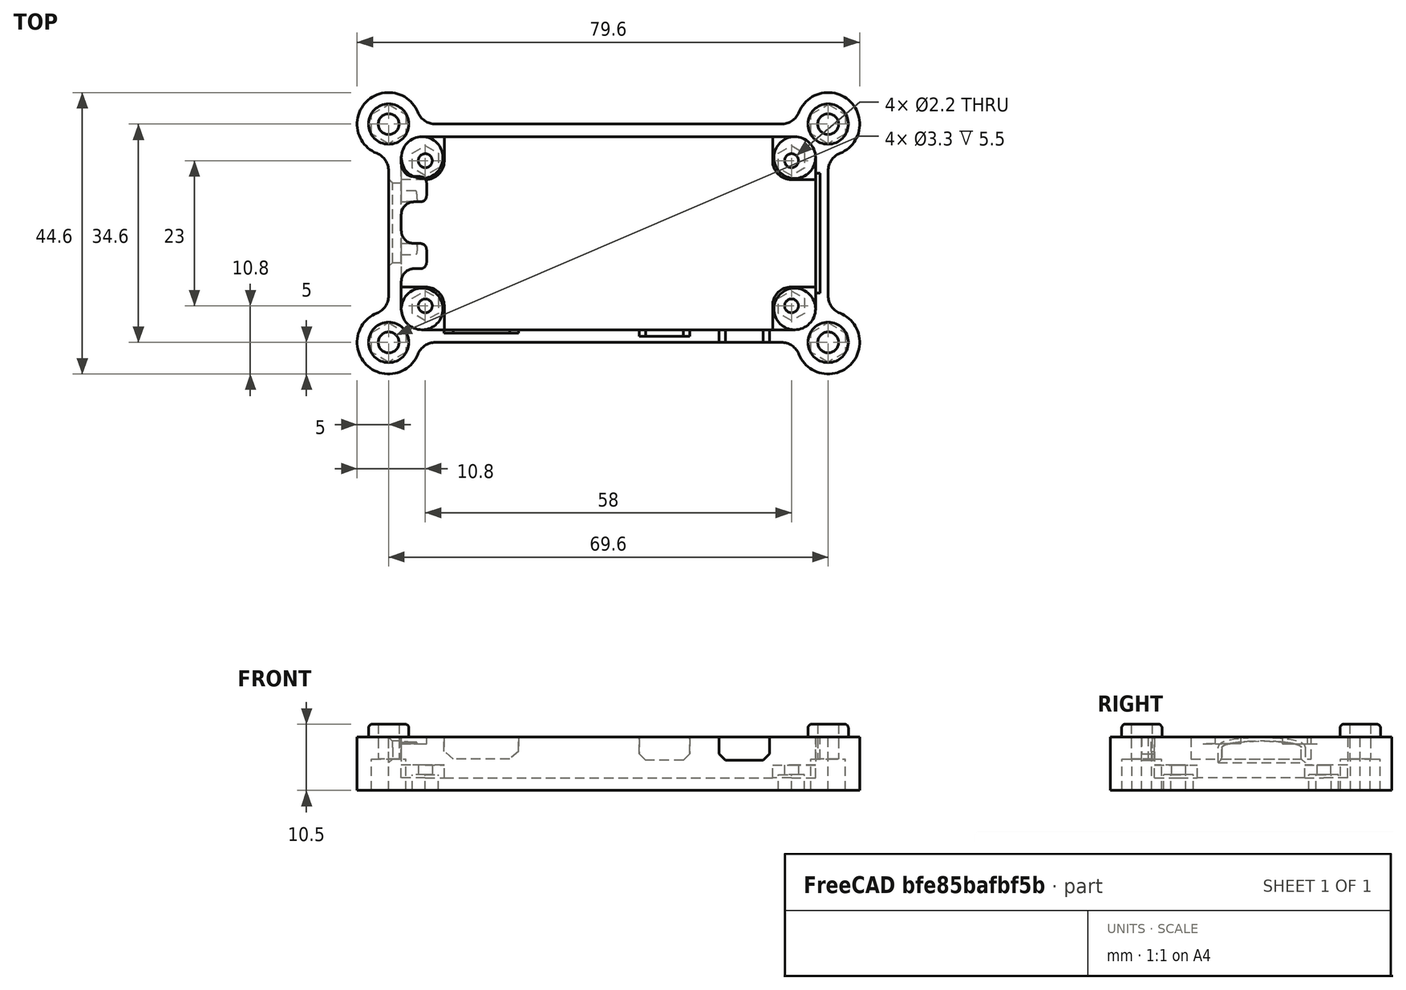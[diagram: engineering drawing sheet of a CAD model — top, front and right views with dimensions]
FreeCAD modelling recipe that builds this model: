
FCSTD DOCUMENT  (FreeCAD 0.18R14111 (Git))
Label: MMDVM_HS_Bottom-SLIM-Single-USB
License: CreativeCommons Attribution-NonCommercial-ShareAlike
LicenseURL: http://creativecommons.org/licenses/by-nc-sa/4.0/
objects: Sketcher::SketchObject×16, PartDesign::Pocket×7, PartDesign::Pad×6, PartDesign::Fillet×5, PartDesign::Hole×2, PartDesign::Chamfer×1, PartDesign::Body×1, Mesh::Feature×1
note: 53 computed .brp shape members not serialized (recipe doc carries the construction recipe); baked Part::Feature solids carry a one-line shape summary decoded from their .brp

FEATURE [Sketcher::SketchObject] Sketch
  MapMode = 5
  Support = -> [XY_Plane]
  sketch-geometry (24):
    g0: LineSegment [constr] StartX=-32.5 StartY=15 StartZ=0 EndX=32.5 EndY=15 EndZ=0
    g1: LineSegment [constr] StartX=32.5 StartY=15 StartZ=0 EndX=32.5 EndY=-15 EndZ=0
    g2: LineSegment [constr] StartX=32.5 StartY=-15 StartZ=0 EndX=-32.5 EndY=-15 EndZ=0
    g3: LineSegment [constr] StartX=-32.5 StartY=-15 StartZ=0 EndX=-32.5 EndY=15 EndZ=0
    g4: LineSegment [constr] StartX=-29 StartY=11.5 StartZ=0 EndX=29 EndY=11.5 EndZ=0
    g5: LineSegment [constr] StartX=29 StartY=11.5 StartZ=0 EndX=29 EndY=-11.5 EndZ=0
    g6: LineSegment [constr] StartX=29 StartY=-11.5 StartZ=0 EndX=-29 EndY=-11.5 EndZ=0
    g7: LineSegment [constr] StartX=-29 StartY=-11.5 StartZ=0 EndX=-29 EndY=11.5 EndZ=0
    g8: Circle CenterX=-29 CenterY=11.5 CenterZ=0 NormalX=0 NormalY=0 NormalZ=1 AngleXU=0 Radius=1.375
    g9: Circle CenterX=29 CenterY=11.5 CenterZ=0 NormalX=0 NormalY=0 NormalZ=1 AngleXU=0 Radius=1.375
    g10: Circle CenterX=29 CenterY=-11.5 CenterZ=0 NormalX=0 NormalY=0 NormalZ=1 AngleXU=0 Radius=1.375
    g11: Circle CenterX=-29 CenterY=-11.5 CenterZ=0 NormalX=0 NormalY=0 NormalZ=1 AngleXU=0 Radius=1.375
    g12: LineSegment [constr] StartX=-29.5 StartY=12 StartZ=0 EndX=29.5 EndY=12 EndZ=0
    g13: LineSegment [constr] StartX=29.5 StartY=12 StartZ=0 EndX=29.5 EndY=-12 EndZ=0
    g14: LineSegment [constr] StartX=29.5 StartY=-12 StartZ=0 EndX=-29.5 EndY=-12 EndZ=0
    g15: LineSegment [constr] StartX=-29.5 StartY=-12 StartZ=0 EndX=-29.5 EndY=12 EndZ=0
    g16: ArcOfCircle CenterX=-29.5 CenterY=12 CenterZ=0 NormalX=0 NormalY=0 NormalZ=1 AngleXU=0 Radius=3 StartAngle=1.5708 EndAngle=3.1416
    g17: ArcOfCircle CenterX=29.5 CenterY=12 CenterZ=0 NormalX=0 NormalY=0 NormalZ=1 AngleXU=0 Radius=3 StartAngle=1.42077e-07 EndAngle=1.5708
    g18: ArcOfCircle CenterX=29.5 CenterY=-12 CenterZ=0 NormalX=0 NormalY=0 NormalZ=1 AngleXU=0 Radius=3 StartAngle=4.71239 EndAngle=6.28319
    g19: ArcOfCircle CenterX=-29.5 CenterY=-12 CenterZ=0 NormalX=0 NormalY=0 NormalZ=1 AngleXU=0 Radius=3 StartAngle=3.14159 EndAngle=4.71239
    g20: LineSegment StartX=-29.5 StartY=15 StartZ=0 EndX=29.5 EndY=15 EndZ=0
    g21: LineSegment StartX=32.5 StartY=12 StartZ=0 EndX=32.5 EndY=-12 EndZ=0
    g22: LineSegment StartX=29.5 StartY=-15 StartZ=0 EndX=-29.5 EndY=-15 EndZ=0
    g23: LineSegment StartX=-32.5 StartY=-12 StartZ=0 EndX=-32.5 EndY=12 EndZ=0
  constraints (68):
    c: Coincident(g0,g1)
    c: Coincident(g1,g2)
    c: Coincident(g2,g3)
    c: Coincident(g3,g0)
    c: Horizontal(g0)
    c: Horizontal(g2)
    c: Vertical(g1)
    c: Vertical(g3)
    c: DistanceX(g0,g0) = 65
    c: DistanceY(g1,g1) = 30
    c: Symmetric(g0,g0,g-2)
    c: Symmetric(g0,g1,g-1)
    c: Coincident(g4,g5)
    c: Coincident(g5,g6)
    c: Coincident(g6,g7)
    c: Coincident(g7,g4)
    c: Horizontal(g4)
    c: Horizontal(g6)
    c: Vertical(g5)
    c: Vertical(g7)
    c: DistanceX(g4,g4) = 58
    c: DistanceY(g5,g5) = 23
    c: Symmetric(g4,g5,g-1)
    c: Symmetric(g4,g4,g-2)
    c: Coincident(g8,g4)
    c: Coincident(g9,g4)
    c: Coincident(g10,g5)
    c: Coincident(g11,g6)
    c: Radius(g11) = 1.375
    c: Radius(g8) = 1.375
    c: Radius(g9) = 1.375
    c: Radius(g10) = 1.375
    c: Coincident(g12,g13)
    c: Coincident(g13,g14)
    c: Coincident(g14,g15)
    c: Coincident(g15,g12)
    c: Horizontal(g12)
    c: Horizontal(g14)
    c: Vertical(g13)
    c: Vertical(g15)
    c: DistanceX(g4,g12) = 0.5
    c: DistanceY(g4,g12) = 0.5
    c: DistanceY(g13,g5) = 0.5
    c: DistanceX(g14,g6) = 0.5
    c: Coincident(g16,g12)
    c: Radius(g16) = 3
    c: Coincident(g17,g12)
    c: Radius(g17) = 3
    c: Coincident(g18,g13)
    c: Radius(g18) = 3
    c: Coincident(g19,g14)
    c: Radius(g19) = 3
    c: PointOnObject(g16,g0)
    c: PointOnObject(g17,g1)
    c: PointOnObject(g18,g2)
    c: PointOnObject(g19,g3)
    c: Coincident(g20,g16)
    c: Horizontal(g20)
    c: Coincident(g20,g17)
    c: Coincident(g21,g17)
    c: Vertical(g21)
    c: Coincident(g18,g21)
    c: Coincident(g22,g18)
    c: Horizontal(g22)
    c: Coincident(g19,g22)
    c: Coincident(g23,g19)
    c: Vertical(g23)
    c: Coincident(g23,g16)
FEATURE [Sketcher::SketchObject] Sketch001
  MapMode = 5
  Support = -> [XY_Plane]
  expr: Constraints[8] = Sketch.Constraints[8]
  expr: Constraints[41] = Sketch.Constraints[41]
  expr: Constraints[9] = Sketch.Constraints[9]
  expr: Constraints[45] = Sketch.Constraints[45]
  expr: Constraints[43] = Sketch.Constraints[43]
  expr: Constraints[42] = Sketch.Constraints[42]
  expr: Constraints[20] = Sketch.Constraints[20]
  expr: Constraints[21] = Sketch.Constraints[21]
  expr: Constraints[28] = Sketch.Constraints[28]
  expr: Constraints[29] = Sketch.Constraints[29]
  expr: Constraints[30] = Sketch.Constraints[30]
  expr: Constraints[40] = Sketch.Constraints[40]
  expr: Constraints[31] = Sketch.Constraints[31]
  expr: Constraints[47] = Sketch.Constraints[47]
  expr: Constraints[49] = Sketch.Constraints[49]
  expr: Constraints[51] = Sketch.Constraints[51]
  sketch-geometry (64):
    g0: LineSegment [constr] StartX=-32.5 StartY=15 StartZ=0 EndX=32.5 EndY=15 EndZ=0
    g1: LineSegment [constr] StartX=32.5 StartY=15 StartZ=0 EndX=32.5 EndY=-15 EndZ=0
    g2: LineSegment [constr] StartX=32.5 StartY=-15 StartZ=0 EndX=-32.5 EndY=-15 EndZ=0
    g3: LineSegment [constr] StartX=-32.5 StartY=-15 StartZ=0 EndX=-32.5 EndY=15 EndZ=0
    g4: LineSegment [constr] StartX=-29 StartY=11.5 StartZ=0 EndX=29 EndY=11.5 EndZ=0
    g5: LineSegment [constr] StartX=29 StartY=11.5 StartZ=0 EndX=29 EndY=-11.5 EndZ=0
    g6: LineSegment [constr] StartX=29 StartY=-11.5 StartZ=0 EndX=-29 EndY=-11.5 EndZ=0
    g7: LineSegment [constr] StartX=-29 StartY=-11.5 StartZ=0 EndX=-29 EndY=11.5 EndZ=0
    g8: Circle [constr] CenterX=-29 CenterY=11.5 CenterZ=0 NormalX=0 NormalY=0 NormalZ=1 AngleXU=0 Radius=1.375
    g9: Circle [constr] CenterX=29 CenterY=11.5 CenterZ=0 NormalX=0 NormalY=0 NormalZ=1 AngleXU=0 Radius=1.375
    g10: Circle [constr] CenterX=29 CenterY=-11.5 CenterZ=0 NormalX=0 NormalY=0 NormalZ=1 AngleXU=0 Radius=1.375
    g11: Circle [constr] CenterX=-29 CenterY=-11.5 CenterZ=0 NormalX=0 NormalY=0 NormalZ=1 AngleXU=0 Radius=1.375
    g12: LineSegment [constr] StartX=-29.5 StartY=12 StartZ=0 EndX=29.5 EndY=12 EndZ=0
    g13: LineSegment [constr] StartX=29.5 StartY=12 StartZ=0 EndX=29.5 EndY=-12 EndZ=0
    g14: LineSegment [constr] StartX=29.5 StartY=-12 StartZ=0 EndX=-29.5 EndY=-12 EndZ=0
    g15: LineSegment [constr] StartX=-29.5 StartY=-12 StartZ=0 EndX=-29.5 EndY=12 EndZ=0
    g16: ArcOfCircle [constr] CenterX=-29.5 CenterY=12 CenterZ=0 NormalX=0 NormalY=0 NormalZ=1 AngleXU=0 Radius=3 StartAngle=1.5708 EndAngle=3.14159
    g17: ArcOfCircle [constr] CenterX=29.5 CenterY=12 CenterZ=0 NormalX=0 NormalY=0 NormalZ=1 AngleXU=0 Radius=3 StartAngle=2.8425e-08 EndAngle=1.5708
    g18: ArcOfCircle [constr] CenterX=29.5 CenterY=-12 CenterZ=0 NormalX=0 NormalY=0 NormalZ=1 AngleXU=0 Radius=3 StartAngle=4.71239 EndAngle=6.28319
    g19: ArcOfCircle [constr] CenterX=-29.5 CenterY=-12 CenterZ=0 NormalX=0 NormalY=0 NormalZ=1 AngleXU=0 Radius=3 StartAngle=3.14159 EndAngle=4.71239
    g20: LineSegment [constr] StartX=-29.5 StartY=15 StartZ=0 EndX=29.5 EndY=15 EndZ=0
    g21: LineSegment [constr] StartX=32.5 StartY=12 StartZ=0 EndX=32.5 EndY=-12 EndZ=0
    g22: LineSegment [constr] StartX=29.5 StartY=-15 StartZ=0 EndX=-29.5 EndY=-15 EndZ=0
    g23: LineSegment [constr] StartX=-32.5 StartY=-12 StartZ=0 EndX=-32.5 EndY=12 EndZ=0
    g24: ArcOfCircle [constr] CenterX=-29.5 CenterY=12 CenterZ=0 NormalX=0 NormalY=0 NormalZ=1 AngleXU=0 Radius=3.3 StartAngle=1.5708 EndAngle=3.14159
    g25: ArcOfCircle [constr] CenterX=29.5 CenterY=12 CenterZ=0 NormalX=0 NormalY=0 NormalZ=1 AngleXU=0 Radius=3.3 StartAngle=-2.2e-10 EndAngle=1.5708
    g26: ArcOfCircle [constr] CenterX=29.5 CenterY=-12 CenterZ=0 NormalX=0 NormalY=0 NormalZ=1 AngleXU=0 Radius=3.3 StartAngle=4.71239 EndAngle=6.28319
    g27: ArcOfCircle [constr] CenterX=-29.5 CenterY=-12 CenterZ=0 NormalX=0 NormalY=0 NormalZ=1 AngleXU=0 Radius=3.3 StartAngle=3.14159 EndAngle=4.71239
    g28: LineSegment [constr] StartX=-32.8 StartY=12 StartZ=0 EndX=-32.8 EndY=-12 EndZ=0
    g29: LineSegment [constr] StartX=-29.5 StartY=15.3 StartZ=0 EndX=29.5 EndY=15.3 EndZ=0
    g30: LineSegment [constr] StartX=32.8 StartY=12 StartZ=0 EndX=32.8 EndY=-12 EndZ=0
    g31: LineSegment [constr] StartX=29.5 StartY=-15.3 StartZ=0 EndX=-29.5 EndY=-15.3 EndZ=0
    g32: LineSegment [constr] StartX=-34.8 StartY=17.3 StartZ=0 EndX=34.8 EndY=17.3 EndZ=0
    g33: LineSegment [constr] StartX=34.8 StartY=17.3 StartZ=0 EndX=34.8 EndY=-17.3 EndZ=0
    g34: LineSegment [constr] StartX=34.8 StartY=-17.3 StartZ=0 EndX=-34.8 EndY=-17.3 EndZ=0
    g35: LineSegment [constr] StartX=-34.8 StartY=-17.3 StartZ=0 EndX=-34.8 EndY=17.3 EndZ=0
    g36: Circle [constr] CenterX=34.8 CenterY=17.3 CenterZ=0 NormalX=0 NormalY=0 NormalZ=1 AngleXU=0 Radius=5
    g37: Circle [constr] CenterX=34.8 CenterY=-17.3 CenterZ=0 NormalX=0 NormalY=0 NormalZ=1 AngleXU=0 Radius=5
    g38: Circle [constr] CenterX=-34.8 CenterY=-17.3 CenterZ=0 NormalX=0 NormalY=0 NormalZ=1 AngleXU=0 Radius=5
    g39: Circle [constr] CenterX=-34.8 CenterY=17.3 CenterZ=0 NormalX=0 NormalY=0 NormalZ=1 AngleXU=0 Radius=5
    g40: Circle [constr] CenterX=27.3838 CenterY=20.3 CenterZ=0 NormalX=0 NormalY=0 NormalZ=1 AngleXU=0 Radius=3
    g41: Circle [constr] CenterX=-27.3838 CenterY=20.3 CenterZ=0 NormalX=0 NormalY=0 NormalZ=1 AngleXU=0 Radius=3
    g42: Circle [constr] CenterX=-37.8 CenterY=9.8838 CenterZ=0 NormalX=0 NormalY=0 NormalZ=1 AngleXU=0 Radius=3
    g43: Circle [constr] CenterX=-37.8 CenterY=-9.8838 CenterZ=0 NormalX=0 NormalY=0 NormalZ=1 AngleXU=0 Radius=3
    g44: Circle [constr] CenterX=-27.3838 CenterY=-20.3 CenterZ=0 NormalX=0 NormalY=0 NormalZ=1 AngleXU=0 Radius=3
    g45: Circle [constr] CenterX=27.3838 CenterY=-20.3 CenterZ=0 NormalX=0 NormalY=0 NormalZ=1 AngleXU=0 Radius=3
    g46: Circle [constr] CenterX=37.8 CenterY=-9.8838 CenterZ=0 NormalX=0 NormalY=0 NormalZ=1 AngleXU=0 Radius=3
    g47: Circle [constr] CenterX=37.8 CenterY=9.8838 CenterZ=0 NormalX=0 NormalY=0 NormalZ=1 AngleXU=0 Radius=3
    g48: ArcOfCircle CenterX=34.8 CenterY=17.3 CenterZ=0 NormalX=0 NormalY=0 NormalZ=1 AngleXU=0 Radius=5 StartAngle=5.09679 EndAngle=9.04038
    g49: ArcOfCircle CenterX=27.3838 CenterY=20.3 CenterZ=0 NormalX=0 NormalY=0 NormalZ=1 AngleXU=0 Radius=3 StartAngle=4.71239 EndAngle=5.89879
    g50: ArcOfCircle CenterX=37.8 CenterY=9.8838 CenterZ=0 NormalX=0 NormalY=0 NormalZ=1 AngleXU=0 Radius=3 StartAngle=1.95519 EndAngle=3.14159
    g51: ArcOfCircle CenterX=37.8 CenterY=-9.8838 CenterZ=0 NormalX=0 NormalY=0 NormalZ=1 AngleXU=0 Radius=3 StartAngle=3.14159 EndAngle=4.32799
    g52: ArcOfCircle CenterX=34.8 CenterY=-17.3 CenterZ=0 NormalX=0 NormalY=0 NormalZ=1 AngleXU=0 Radius=5 StartAngle=3.52599 EndAngle=7.46958
    g53: ArcOfCircle CenterX=27.3838 CenterY=-20.3 CenterZ=0 NormalX=0 NormalY=0 NormalZ=1 AngleXU=0 Radius=3 StartAngle=0.384397 EndAngle=1.5708
    g54: ArcOfCircle CenterX=-27.3838 CenterY=-20.3 CenterZ=0 NormalX=0 NormalY=0 NormalZ=1 AngleXU=0 Radius=3 StartAngle=1.5708 EndAngle=2.7572
    g55: ArcOfCircle CenterX=-34.8 CenterY=-17.3 CenterZ=0 NormalX=0 NormalY=0 NormalZ=1 AngleXU=0 Radius=5 StartAngle=1.95519 EndAngle=5.89879
    g56: ArcOfCircle CenterX=-37.8 CenterY=-9.8838 CenterZ=0 NormalX=0 NormalY=0 NormalZ=1 AngleXU=0 Radius=3 StartAngle=5.09679 EndAngle=6.28319
    g57: ArcOfCircle CenterX=-37.8 CenterY=9.8838 CenterZ=0 NormalX=0 NormalY=0 NormalZ=1 AngleXU=0 Radius=3 StartAngle=6.28319 EndAngle=7.46958
    g58: ArcOfCircle CenterX=-34.8 CenterY=17.3 CenterZ=0 NormalX=0 NormalY=0 NormalZ=1 AngleXU=0 Radius=5 StartAngle=0.384397 EndAngle=4.32799
    g59: ArcOfCircle CenterX=-27.3838 CenterY=20.3 CenterZ=0 NormalX=0 NormalY=0 NormalZ=1 AngleXU=0 Radius=3 StartAngle=3.52599 EndAngle=4.71239
    g60: LineSegment StartX=-27.3838 StartY=17.3 StartZ=0 EndX=27.3838 EndY=17.3 EndZ=0
    g61: LineSegment StartX=34.8 StartY=9.8838 StartZ=0 EndX=34.8 EndY=-9.8838 EndZ=0
    g62: LineSegment StartX=27.3838 StartY=-17.3 StartZ=0 EndX=-27.3838 EndY=-17.3 EndZ=0
    g63: LineSegment StartX=-34.8 StartY=-9.8838 StartZ=0 EndX=-34.8 EndY=9.8838 EndZ=0
  constraints (184):
    c: Coincident(g0,g1)
    c: Coincident(g1,g2)
    c: Coincident(g2,g3)
    c: Coincident(g3,g0)
    c: Horizontal(g0)
    c: Horizontal(g2)
    c: Vertical(g1)
    c: Vertical(g3)
    c: DistanceX(g0,g0) = 65
    c: DistanceY(g1,g1) = 30
    c: Symmetric(g0,g0,g-2)
    c: Symmetric(g0,g1,g-1)
    c: Coincident(g4,g5)
    c: Coincident(g5,g6)
    c: Coincident(g6,g7)
    c: Coincident(g7,g4)
    c: Horizontal(g4)
    c: Horizontal(g6)
    c: Vertical(g5)
    c: Vertical(g7)
    c: DistanceX(g4,g4) = 58
    c: DistanceY(g5,g5) = 23
    c: Symmetric(g4,g5,g-1)
    c: Symmetric(g4,g4,g-2)
    c: Coincident(g8,g4)
    c: Coincident(g9,g4)
    c: Coincident(g10,g5)
    c: Coincident(g11,g6)
    c: Radius(g11) = 1.375
    c: Radius(g8) = 1.375
    c: Radius(g9) = 1.375
    c: Radius(g10) = 1.375
    c: Coincident(g12,g13)
    c: Coincident(g13,g14)
    c: Coincident(g14,g15)
    c: Coincident(g15,g12)
    c: Horizontal(g12)
    c: Horizontal(g14)
    c: Vertical(g13)
    c: Vertical(g15)
    c: DistanceX(g4,g12) = 0.5
    c: DistanceY(g4,g12) = 0.5
    c: DistanceY(g13,g5) = 0.5
    c: DistanceX(g14,g6) = 0.5
    c: Coincident(g16,g12)
    c: Radius(g16) = 3
    c: Coincident(g17,g12)
    c: Radius(g17) = 3
    c: Coincident(g18,g13)
    c: Radius(g18) = 3
    c: Coincident(g19,g14)
    c: Radius(g19) = 3
    c: PointOnObject(g16,g0)
    c: PointOnObject(g17,g1)
    c: PointOnObject(g18,g2)
    c: PointOnObject(g19,g3)
    c: Coincident(g20,g16)
    c: Horizontal(g20)
    c: Coincident(g20,g17)
    c: Coincident(g21,g17)
    c: Vertical(g21)
    c: Coincident(g18,g21)
    c: Coincident(g22,g18)
    c: Horizontal(g22)
    c: Coincident(g19,g22)
    c: Coincident(g23,g19)
    c: Vertical(g23)
    c: Coincident(g23,g16)
    c: Coincident(g24,g12)
    c: Radius(g24) = 3.3
    c: Coincident(g25,g12)
    c: Radius(g25) = 3.3
    c: Coincident(g26,g13)
    c: Radius(g26) = 3.3
    c: Coincident(g27,g14)
    c: Radius(g27) = 3.3
    c: Vertical(g28)
    c: DistanceX(g28,g2) = 0.3
    c: Coincident(g27,g28)
    c: Coincident(g28,g24)
    c: Horizontal(g29)
    c: DistanceY(g0,g29) = 0.3
    c: Coincident(g24,g29)
    c: Coincident(g25,g29)
    c: Vertical(g30)
    c: DistanceX(g0,g30) = 0.3
    c: Coincident(g25,g30)
    c: Coincident(g30,g26)
    c: Horizontal(g31)
    c: DistanceY(g31,g1) = 0.3
    c: Coincident(g31,g26)
    c: Coincident(g31,g27)
    c: Coincident(g32,g33)
    c: Coincident(g33,g34)
    c: Coincident(g34,g35)
    c: Coincident(g35,g32)
    c: Horizontal(g32)
    c: Horizontal(g34)
    c: Vertical(g33)
    c: Vertical(g35)
    c: DistanceY(g25,g32) = 2
    c: DistanceX(g25,g32) = 2
    c: DistanceY(g33,g26) = 2
    c: DistanceX(g34,g27) = 2
    c: Coincident(g36,g32)
    c: Coincident(g37,g33)
    c: Coincident(g38,g34)
    c: Coincident(g39,g32)
    c: Radius(g39) = 5
    c: Radius(g38) = 5
    c: Radius(g37) = 5
    c: Radius(g36) = 5
    c: Radius(g40) = 3
    c: Tangent(g40,g36)
    c: Tangent(g40,g32)
    c: Tangent(g47,g36)
    c: Radius(g47) = 3
    c: Tangent(g47,g33)
    c: Radius(g46) = 3
    c: Tangent(g46,g37)
    c: Tangent(g46,g33)
    c: Radius(g45) = 3
    c: Tangent(g45,g37)
    c: Tangent(g45,g34)
    c: Radius(g44) = 3
    c: Tangent(g44,g34)
    c: Tangent(g44,g38)
    c: Radius(g43) = 3
    c: Tangent(g43,g38)
    c: Tangent(g43,g35)
    c: Radius(g42) = 3
    c: Tangent(g42,g35)
    c: Tangent(g42,g39)
    c: Radius(g41) = 3
    c: Tangent(g41,g32)
    c: Tangent(g41,g39)
    c: Coincident(g48,g32)
    c: PointOnObject(g48,g36)
    c: Coincident(g49,g40)
    c: PointOnObject(g49,g40)
    c: Coincident(g50,g47)
    c: PointOnObject(g50,g47)
    c: Coincident(g51,g46)
    c: PointOnObject(g51,g46)
    c: Coincident(g52,g33)
    c: PointOnObject(g52,g37)
    c: Coincident(g53,g45)
    c: PointOnObject(g53,g45)
    c: Coincident(g54,g44)
    c: PointOnObject(g54,g44)
    c: Coincident(g55,g34)
    c: PointOnObject(g55,g38)
    c: Coincident(g56,g43)
    c: PointOnObject(g56,g43)
    c: Coincident(g57,g42)
    c: PointOnObject(g57,g42)
    c: Coincident(g58,g32)
    c: PointOnObject(g58,g39)
    c: Coincident(g59,g41)
    c: PointOnObject(g59,g41)
    c: Coincident(g49,g48)
    c: Coincident(g48,g50)
    c: Coincident(g51,g52)
    c: Coincident(g52,g53)
    c: Coincident(g54,g55)
    c: Coincident(g55,g56)
    c: Coincident(g57,g58)
    c: Coincident(g58,g59)
    c: PointOnObject(g60,g32)
    c: Horizontal(g60)
    c: PointOnObject(g61,g33)
    c: Vertical(g61)
    c: PointOnObject(g62,g34)
    c: Horizontal(g62)
    c: PointOnObject(g63,g35)
    c: Vertical(g63)
    c: Coincident(g59,g60)
    c: Coincident(g60,g49)
    c: Coincident(g50,g61)
    c: Coincident(g61,g51)
    c: Coincident(g53,g62)
    c: Coincident(g54,g62)
    c: Coincident(g56,g63)
    c: Coincident(g57,g63)
FEATURE [PartDesign::Pad] Pad
  Length = 8.5
  Length2 = 100
  Profile = -> Sketch001
  Type = 0
FEATURE [Sketcher::SketchObject] Sketch002
  MapMode = 5
  Placement = pos=(0,0,8.5) rot=(0,0,1;0rad)
  Support = -> [Pad]
  expr: Constraints[133] = Sketch001.Constraints[133]
  expr: Constraints[130] = Sketch001.Constraints[130]
  expr: Constraints[112] = Sketch001.Constraints[112]
  expr: Constraints[124] = Sketch001.Constraints[124]
  expr: Constraints[127] = Sketch001.Constraints[127]
  expr: Constraints[110] = Sketch001.Constraints[110]
  expr: Constraints[51] = Sketch001.Constraints[51]
  expr: Constraints[100] = Sketch001.Constraints[100]
  expr: Constraints[77] = Sketch001.Constraints[77]
  expr: Constraints[89] = Sketch001.Constraints[89]
  expr: Constraints[85] = Sketch001.Constraints[85]
  expr: Constraints[118] = Sketch001.Constraints[118]
  expr: Constraints[71] = Sketch001.Constraints[71]
  expr: Constraints[111] = Sketch001.Constraints[111]
  expr: Constraints[103] = Sketch001.Constraints[103]
  expr: Constraints[49] = Sketch001.Constraints[49]
  expr: Constraints[102] = Sketch001.Constraints[102]
  expr: Constraints[69] = Sketch001.Constraints[69]
  expr: Constraints[47] = Sketch001.Constraints[47]
  expr: Constraints[73] = Sketch001.Constraints[73]
  expr: Constraints[75] = Sketch001.Constraints[75]
  expr: Constraints[31] = Sketch001.Constraints[31]
  expr: Constraints[116] = Sketch001.Constraints[116]
  expr: Constraints[40] = Sketch001.Constraints[40]
  expr: Constraints[30] = Sketch001.Constraints[30]
  expr: Constraints[29] = Sketch001.Constraints[29]
  expr: Constraints[28] = Sketch001.Constraints[28]
  expr: Constraints[121] = Sketch001.Constraints[121]
  expr: Constraints[21] = Sketch001.Constraints[21]
  expr: Constraints[20] = Sketch001.Constraints[20]
  expr: Constraints[43] = Sketch001.Constraints[43]
  expr: Constraints[42] = Sketch001.Constraints[42]
  expr: Constraints[101] = Sketch001.Constraints[101]
  expr: Constraints[108] = Sketch001.Constraints[108]
  expr: Constraints[45] = Sketch001.Constraints[45]
  expr: Constraints[41] = Sketch001.Constraints[41]
  expr: Constraints[9] = Sketch001.Constraints[9]
  expr: Constraints[81] = Sketch001.Constraints[81]
  expr: Constraints[109] = Sketch001.Constraints[109]
  expr: Constraints[8] = Sketch001.Constraints[8]
  sketch-geometry (64):
    g0: LineSegment [constr] StartX=-32.5 StartY=15 StartZ=0 EndX=32.5 EndY=15 EndZ=0
    g1: LineSegment [constr] StartX=32.5 StartY=15 StartZ=0 EndX=32.5 EndY=-15 EndZ=0
    g2: LineSegment [constr] StartX=32.5 StartY=-15 StartZ=0 EndX=-32.5 EndY=-15 EndZ=0
    g3: LineSegment [constr] StartX=-32.5 StartY=-15 StartZ=0 EndX=-32.5 EndY=15 EndZ=0
    g4: LineSegment [constr] StartX=-29 StartY=11.5 StartZ=0 EndX=29 EndY=11.5 EndZ=0
    g5: LineSegment [constr] StartX=29 StartY=11.5 StartZ=0 EndX=29 EndY=-11.5 EndZ=0
    g6: LineSegment [constr] StartX=29 StartY=-11.5 StartZ=0 EndX=-29 EndY=-11.5 EndZ=0
    g7: LineSegment [constr] StartX=-29 StartY=-11.5 StartZ=0 EndX=-29 EndY=11.5 EndZ=0
    g8: Circle [constr] CenterX=-29 CenterY=11.5 CenterZ=0 NormalX=0 NormalY=0 NormalZ=1 AngleXU=0 Radius=1.375
    g9: Circle [constr] CenterX=29 CenterY=11.5 CenterZ=0 NormalX=0 NormalY=0 NormalZ=1 AngleXU=0 Radius=1.375
    g10: Circle [constr] CenterX=29 CenterY=-11.5 CenterZ=0 NormalX=0 NormalY=0 NormalZ=1 AngleXU=0 Radius=1.375
    g11: Circle [constr] CenterX=-29 CenterY=-11.5 CenterZ=0 NormalX=0 NormalY=0 NormalZ=1 AngleXU=0 Radius=1.375
    g12: LineSegment [constr] StartX=-29.5 StartY=12 StartZ=0 EndX=29.5 EndY=12 EndZ=0
    g13: LineSegment [constr] StartX=29.5 StartY=12 StartZ=0 EndX=29.5 EndY=-12 EndZ=0
    g14: LineSegment [constr] StartX=29.5 StartY=-12 StartZ=0 EndX=-29.5 EndY=-12 EndZ=0
    g15: LineSegment [constr] StartX=-29.5 StartY=-12 StartZ=0 EndX=-29.5 EndY=12 EndZ=0
    g16: ArcOfCircle [constr] CenterX=-29.5 CenterY=12 CenterZ=0 NormalX=0 NormalY=0 NormalZ=1 AngleXU=0 Radius=3 StartAngle=1.5708 EndAngle=3.14159
    g17: ArcOfCircle [constr] CenterX=29.5 CenterY=12 CenterZ=0 NormalX=0 NormalY=0 NormalZ=1 AngleXU=0 Radius=3 StartAngle=2.8425e-08 EndAngle=1.5708
    g18: ArcOfCircle [constr] CenterX=29.5 CenterY=-12 CenterZ=0 NormalX=0 NormalY=0 NormalZ=1 AngleXU=0 Radius=3 StartAngle=4.71239 EndAngle=6.28319
    g19: ArcOfCircle [constr] CenterX=-29.5 CenterY=-12 CenterZ=0 NormalX=0 NormalY=0 NormalZ=1 AngleXU=0 Radius=3 StartAngle=3.14159 EndAngle=4.71239
    g20: LineSegment [constr] StartX=-29.5 StartY=15 StartZ=0 EndX=29.5 EndY=15 EndZ=0
    g21: LineSegment [constr] StartX=32.5 StartY=12 StartZ=0 EndX=32.5 EndY=-12 EndZ=0
    g22: LineSegment [constr] StartX=29.5 StartY=-15 StartZ=0 EndX=-29.5 EndY=-15 EndZ=0
    g23: LineSegment [constr] StartX=-32.5 StartY=-12 StartZ=0 EndX=-32.5 EndY=12 EndZ=0
    g24: ArcOfCircle CenterX=-29.5 CenterY=12 CenterZ=0 NormalX=0 NormalY=0 NormalZ=1 AngleXU=0 Radius=3.3 StartAngle=1.5708 EndAngle=3.14159
    g25: ArcOfCircle CenterX=29.5 CenterY=12 CenterZ=0 NormalX=0 NormalY=0 NormalZ=1 AngleXU=0 Radius=3.3 StartAngle=-2.2e-10 EndAngle=1.5708
    g26: ArcOfCircle CenterX=29.5 CenterY=-12 CenterZ=0 NormalX=0 NormalY=0 NormalZ=1 AngleXU=0 Radius=3.3 StartAngle=4.71239 EndAngle=6.28319
    g27: ArcOfCircle CenterX=-29.5 CenterY=-12 CenterZ=0 NormalX=0 NormalY=0 NormalZ=1 AngleXU=0 Radius=3.3 StartAngle=3.14159 EndAngle=4.71239
    g28: LineSegment StartX=-32.8 StartY=12 StartZ=0 EndX=-32.8 EndY=-12 EndZ=0
    g29: LineSegment StartX=-29.5 StartY=15.3 StartZ=0 EndX=29.5 EndY=15.3 EndZ=0
    g30: LineSegment StartX=32.8 StartY=12 StartZ=0 EndX=32.8 EndY=-12 EndZ=0
    g31: LineSegment StartX=29.5 StartY=-15.3 StartZ=0 EndX=-29.5 EndY=-15.3 EndZ=0
    g32: LineSegment [constr] StartX=-34.8 StartY=17.3 StartZ=0 EndX=34.8 EndY=17.3 EndZ=0
    g33: LineSegment [constr] StartX=34.8 StartY=17.3 StartZ=0 EndX=34.8 EndY=-17.3 EndZ=0
    g34: LineSegment [constr] StartX=34.8 StartY=-17.3 StartZ=0 EndX=-34.8 EndY=-17.3 EndZ=0
    g35: LineSegment [constr] StartX=-34.8 StartY=-17.3 StartZ=0 EndX=-34.8 EndY=17.3 EndZ=0
    g36: Circle [constr] CenterX=34.8 CenterY=17.3 CenterZ=0 NormalX=0 NormalY=0 NormalZ=1 AngleXU=0 Radius=5
    g37: Circle [constr] CenterX=34.8 CenterY=-17.3 CenterZ=0 NormalX=0 NormalY=0 NormalZ=1 AngleXU=0 Radius=5
    g38: Circle [constr] CenterX=-34.8 CenterY=-17.3 CenterZ=0 NormalX=0 NormalY=0 NormalZ=1 AngleXU=0 Radius=5
    g39: Circle [constr] CenterX=-34.8 CenterY=17.3 CenterZ=0 NormalX=0 NormalY=0 NormalZ=1 AngleXU=0 Radius=5
    g40: Circle [constr] CenterX=27.3838 CenterY=20.3 CenterZ=0 NormalX=0 NormalY=0 NormalZ=1 AngleXU=0 Radius=3
    g41: Circle [constr] CenterX=-27.3838 CenterY=20.3 CenterZ=0 NormalX=0 NormalY=0 NormalZ=1 AngleXU=0 Radius=3
    g42: Circle [constr] CenterX=-37.8 CenterY=9.8838 CenterZ=0 NormalX=0 NormalY=0 NormalZ=1 AngleXU=0 Radius=3
    g43: Circle [constr] CenterX=-37.8 CenterY=-9.8838 CenterZ=0 NormalX=0 NormalY=0 NormalZ=1 AngleXU=0 Radius=3
    g44: Circle [constr] CenterX=-27.3838 CenterY=-20.3 CenterZ=0 NormalX=0 NormalY=0 NormalZ=1 AngleXU=0 Radius=3
    g45: Circle [constr] CenterX=27.3838 CenterY=-20.3 CenterZ=0 NormalX=0 NormalY=0 NormalZ=1 AngleXU=0 Radius=3
    g46: Circle [constr] CenterX=37.8 CenterY=-9.8838 CenterZ=0 NormalX=0 NormalY=0 NormalZ=1 AngleXU=0 Radius=3
    g47: Circle [constr] CenterX=37.8 CenterY=9.8838 CenterZ=0 NormalX=0 NormalY=0 NormalZ=1 AngleXU=0 Radius=3
    g48: ArcOfCircle [constr] CenterX=34.8 CenterY=17.3 CenterZ=0 NormalX=0 NormalY=0 NormalZ=1 AngleXU=0 Radius=5 StartAngle=5.09679 EndAngle=9.04038
    g49: ArcOfCircle [constr] CenterX=27.3838 CenterY=20.3 CenterZ=0 NormalX=0 NormalY=0 NormalZ=1 AngleXU=0 Radius=3 StartAngle=4.71239 EndAngle=5.89879
    g50: ArcOfCircle [constr] CenterX=37.8 CenterY=9.8838 CenterZ=0 NormalX=0 NormalY=0 NormalZ=1 AngleXU=0 Radius=3 StartAngle=1.95519 EndAngle=3.14159
    g51: ArcOfCircle [constr] CenterX=37.8 CenterY=-9.8838 CenterZ=0 NormalX=0 NormalY=0 NormalZ=1 AngleXU=0 Radius=3 StartAngle=3.14159 EndAngle=4.32799
    g52: ArcOfCircle [constr] CenterX=34.8 CenterY=-17.3 CenterZ=0 NormalX=0 NormalY=0 NormalZ=1 AngleXU=0 Radius=5 StartAngle=3.52599 EndAngle=7.46958
    g53: ArcOfCircle [constr] CenterX=27.3838 CenterY=-20.3 CenterZ=0 NormalX=0 NormalY=0 NormalZ=1 AngleXU=0 Radius=3 StartAngle=0.384397 EndAngle=1.5708
    g54: ArcOfCircle [constr] CenterX=-27.3838 CenterY=-20.3 CenterZ=0 NormalX=0 NormalY=0 NormalZ=1 AngleXU=0 Radius=3 StartAngle=1.5708 EndAngle=2.7572
    g55: ArcOfCircle [constr] CenterX=-34.8 CenterY=-17.3 CenterZ=0 NormalX=0 NormalY=0 NormalZ=1 AngleXU=0 Radius=5 StartAngle=1.95519 EndAngle=5.89879
    g56: ArcOfCircle [constr] CenterX=-37.8 CenterY=-9.8838 CenterZ=0 NormalX=0 NormalY=0 NormalZ=1 AngleXU=0 Radius=3 StartAngle=5.09679 EndAngle=6.28319
    g57: ArcOfCircle [constr] CenterX=-37.8 CenterY=9.8838 CenterZ=0 NormalX=0 NormalY=0 NormalZ=1 AngleXU=0 Radius=3 StartAngle=6.28319 EndAngle=7.46958
    g58: ArcOfCircle [constr] CenterX=-34.8 CenterY=17.3 CenterZ=0 NormalX=0 NormalY=0 NormalZ=1 AngleXU=0 Radius=5 StartAngle=0.384397 EndAngle=4.32799
    g59: ArcOfCircle [constr] CenterX=-27.3838 CenterY=20.3 CenterZ=0 NormalX=0 NormalY=0 NormalZ=1 AngleXU=0 Radius=3 StartAngle=3.52599 EndAngle=4.71239
    g60: LineSegment [constr] StartX=-27.3838 StartY=17.3 StartZ=0 EndX=27.3838 EndY=17.3 EndZ=0
    g61: LineSegment [constr] StartX=34.8 StartY=9.8838 StartZ=0 EndX=34.8 EndY=-9.8838 EndZ=0
    g62: LineSegment [constr] StartX=27.3838 StartY=-17.3 StartZ=0 EndX=-27.3838 EndY=-17.3 EndZ=0
    g63: LineSegment [constr] StartX=-34.8 StartY=-9.8838 StartZ=0 EndX=-34.8 EndY=9.8838 EndZ=0
  constraints (184):
    c: Coincident(g0,g1)
    c: Coincident(g1,g2)
    c: Coincident(g2,g3)
    c: Coincident(g3,g0)
    c: Horizontal(g0)
    c: Horizontal(g2)
    c: Vertical(g1)
    c: Vertical(g3)
    c: DistanceX(g0,g0) = 65
    c: DistanceY(g1,g1) = 30
    c: Symmetric(g0,g0,g-2)
    c: Symmetric(g0,g1,g-1)
    c: Coincident(g4,g5)
    c: Coincident(g5,g6)
    c: Coincident(g6,g7)
    c: Coincident(g7,g4)
    c: Horizontal(g4)
    c: Horizontal(g6)
    c: Vertical(g5)
    c: Vertical(g7)
    c: DistanceX(g4,g4) = 58
    c: DistanceY(g5,g5) = 23
    c: Symmetric(g4,g5,g-1)
    c: Symmetric(g4,g4,g-2)
    c: Coincident(g8,g4)
    c: Coincident(g9,g4)
    c: Coincident(g10,g5)
    c: Coincident(g11,g6)
    c: Radius(g11) = 1.375
    c: Radius(g8) = 1.375
    c: Radius(g9) = 1.375
    c: Radius(g10) = 1.375
    c: Coincident(g12,g13)
    c: Coincident(g13,g14)
    c: Coincident(g14,g15)
    c: Coincident(g15,g12)
    c: Horizontal(g12)
    c: Horizontal(g14)
    c: Vertical(g13)
    c: Vertical(g15)
    c: DistanceX(g4,g12) = 0.5
    c: DistanceY(g4,g12) = 0.5
    c: DistanceY(g13,g5) = 0.5
    c: DistanceX(g14,g6) = 0.5
    c: Coincident(g16,g12)
    c: Radius(g16) = 3
    c: Coincident(g17,g12)
    c: Radius(g17) = 3
    c: Coincident(g18,g13)
    c: Radius(g18) = 3
    c: Coincident(g19,g14)
    c: Radius(g19) = 3
    c: PointOnObject(g16,g0)
    c: PointOnObject(g17,g1)
    c: PointOnObject(g18,g2)
    c: PointOnObject(g19,g3)
    c: Coincident(g20,g16)
    c: Horizontal(g20)
    c: Coincident(g20,g17)
    c: Coincident(g21,g17)
    c: Vertical(g21)
    c: Coincident(g18,g21)
    c: Coincident(g22,g18)
    c: Horizontal(g22)
    c: Coincident(g19,g22)
    c: Coincident(g23,g19)
    c: Vertical(g23)
    c: Coincident(g23,g16)
    c: Coincident(g24,g12)
    c: Radius(g24) = 3.3
    c: Coincident(g25,g12)
    c: Radius(g25) = 3.3
    c: Coincident(g26,g13)
    c: Radius(g26) = 3.3
    c: Coincident(g27,g14)
    c: Radius(g27) = 3.3
    c: Vertical(g28)
    c: DistanceX(g28,g2) = 0.3
    c: Coincident(g27,g28)
    c: Coincident(g28,g24)
    c: Horizontal(g29)
    c: DistanceY(g0,g29) = 0.3
    c: Coincident(g24,g29)
    c: Coincident(g25,g29)
    c: Vertical(g30)
    c: DistanceX(g0,g30) = 0.3
    c: Coincident(g25,g30)
    c: Coincident(g30,g26)
    c: Horizontal(g31)
    c: DistanceY(g31,g1) = 0.3
    c: Coincident(g31,g26)
    c: Coincident(g31,g27)
    c: Coincident(g32,g33)
    c: Coincident(g33,g34)
    c: Coincident(g34,g35)
    c: Coincident(g35,g32)
    c: Horizontal(g32)
    c: Horizontal(g34)
    c: Vertical(g33)
    c: Vertical(g35)
    c: DistanceY(g25,g32) = 2
    c: DistanceX(g25,g32) = 2
    c: DistanceY(g33,g26) = 2
    c: DistanceX(g34,g27) = 2
    c: Coincident(g36,g32)
    c: Coincident(g37,g33)
    c: Coincident(g38,g34)
    c: Coincident(g39,g32)
    c: Radius(g39) = 5
    c: Radius(g38) = 5
    c: Radius(g37) = 5
    c: Radius(g36) = 5
    c: Radius(g40) = 3
    c: Tangent(g40,g36)
    c: Tangent(g40,g32)
    c: Tangent(g47,g36)
    c: Radius(g47) = 3
    c: Tangent(g47,g33)
    c: Radius(g46) = 3
    c: Tangent(g46,g37)
    c: Tangent(g46,g33)
    c: Radius(g45) = 3
    c: Tangent(g45,g37)
    c: Tangent(g45,g34)
    c: Radius(g44) = 3
    c: Tangent(g44,g34)
    c: Tangent(g44,g38)
    c: Radius(g43) = 3
    c: Tangent(g43,g38)
    c: Tangent(g43,g35)
    c: Radius(g42) = 3
    c: Tangent(g42,g35)
    c: Tangent(g42,g39)
    c: Radius(g41) = 3
    c: Tangent(g41,g32)
    c: Tangent(g41,g39)
    c: Coincident(g48,g32)
    c: PointOnObject(g48,g36)
    c: Coincident(g49,g40)
    c: PointOnObject(g49,g40)
    c: Coincident(g50,g47)
    c: PointOnObject(g50,g47)
    c: Coincident(g51,g46)
    c: PointOnObject(g51,g46)
    c: Coincident(g52,g33)
    c: PointOnObject(g52,g37)
    c: Coincident(g53,g45)
    c: PointOnObject(g53,g45)
    c: Coincident(g54,g44)
    c: PointOnObject(g54,g44)
    c: Coincident(g55,g34)
    c: PointOnObject(g55,g38)
    c: Coincident(g56,g43)
    c: PointOnObject(g56,g43)
    c: Coincident(g57,g42)
    c: PointOnObject(g57,g42)
    c: Coincident(g58,g32)
    c: PointOnObject(g58,g39)
    c: Coincident(g59,g41)
    c: PointOnObject(g59,g41)
    c: Coincident(g49,g48)
    c: Coincident(g48,g50)
    c: Coincident(g51,g52)
    c: Coincident(g52,g53)
    c: Coincident(g54,g55)
    c: Coincident(g55,g56)
    c: Coincident(g57,g58)
    c: Coincident(g58,g59)
    c: PointOnObject(g60,g32)
    c: Horizontal(g60)
    c: PointOnObject(g61,g33)
    c: Vertical(g61)
    c: PointOnObject(g62,g34)
    c: Horizontal(g62)
    c: PointOnObject(g63,g35)
    c: Vertical(g63)
    c: Coincident(g59,g60)
    c: Coincident(g60,g49)
    c: Coincident(g50,g61)
    c: Coincident(g61,g51)
    c: Coincident(g53,g62)
    c: Coincident(g54,g62)
    c: Coincident(g56,g63)
    c: Coincident(g57,g63)
FEATURE [PartDesign::Pocket] Pocket
  BaseFeature = -> Pad
  Length = 6.5
  Length2 = 100
  Profile = -> Sketch002
  Type = 0
FEATURE [Sketcher::SketchObject] Sketch003
  MapMode = 5
  Placement = pos=(0,0,2) rot=(0,0,1;0rad)
  Support = -> [Pocket]
  expr: Constraints[133] = Sketch002.Constraints[133]
  expr: Constraints[130] = Sketch002.Constraints[130]
  expr: Constraints[112] = Sketch002.Constraints[112]
  expr: Constraints[127] = Sketch002.Constraints[127]
  expr: Constraints[124] = Sketch002.Constraints[124]
  expr: Constraints[110] = Sketch002.Constraints[110]
  expr: Constraints[51] = Sketch002.Constraints[51]
  expr: Constraints[100] = Sketch002.Constraints[100]
  expr: Constraints[77] = Sketch002.Constraints[77]
  expr: Constraints[89] = Sketch002.Constraints[89]
  expr: Constraints[85] = Sketch002.Constraints[85]
  expr: Constraints[118] = Sketch002.Constraints[118]
  expr: Constraints[111] = Sketch002.Constraints[111]
  expr: Constraints[103] = Sketch002.Constraints[103]
  expr: Constraints[71] = Sketch002.Constraints[71]
  expr: Constraints[102] = Sketch002.Constraints[102]
  expr: Constraints[49] = Sketch002.Constraints[49]
  expr: Constraints[69] = Sketch002.Constraints[69]
  expr: Constraints[75] = Sketch002.Constraints[75]
  expr: Constraints[73] = Sketch002.Constraints[73]
  expr: Constraints[47] = Sketch002.Constraints[47]
  expr: Constraints[31] = Sketch002.Constraints[31]
  expr: Constraints[40] = Sketch002.Constraints[40]
  expr: Constraints[116] = Sketch002.Constraints[116]
  expr: Constraints[30] = Sketch002.Constraints[30]
  expr: Constraints[29] = Sketch002.Constraints[29]
  expr: Constraints[121] = Sketch002.Constraints[121]
  expr: Constraints[28] = Sketch002.Constraints[28]
  expr: Constraints[21] = Sketch002.Constraints[21]
  expr: Constraints[20] = Sketch002.Constraints[20]
  expr: Constraints[43] = Sketch002.Constraints[43]
  expr: Constraints[42] = Sketch002.Constraints[42]
  expr: Constraints[101] = Sketch002.Constraints[101]
  expr: Constraints[45] = Sketch002.Constraints[45]
  expr: Constraints[108] = Sketch002.Constraints[108]
  expr: Constraints[41] = Sketch002.Constraints[41]
  expr: Constraints[9] = Sketch002.Constraints[9]
  expr: Constraints[81] = Sketch002.Constraints[81]
  expr: Constraints[109] = Sketch002.Constraints[109]
  expr: Constraints[8] = Sketch002.Constraints[8]
  sketch-geometry (92):
    g0: LineSegment [constr] StartX=-32.5 StartY=15 StartZ=0 EndX=32.5 EndY=15 EndZ=0
    g1: LineSegment [constr] StartX=32.5 StartY=15 StartZ=0 EndX=32.5 EndY=-15 EndZ=0
    g2: LineSegment [constr] StartX=32.5 StartY=-15 StartZ=0 EndX=-32.5 EndY=-15 EndZ=0
    g3: LineSegment [constr] StartX=-32.5 StartY=-15 StartZ=0 EndX=-32.5 EndY=15 EndZ=0
    g4: LineSegment [constr] StartX=-29 StartY=11.5 StartZ=0 EndX=29 EndY=11.5 EndZ=0
    g5: LineSegment [constr] StartX=29 StartY=11.5 StartZ=0 EndX=29 EndY=-11.5 EndZ=0
    g6: LineSegment [constr] StartX=29 StartY=-11.5 StartZ=0 EndX=-29 EndY=-11.5 EndZ=0
    g7: LineSegment [constr] StartX=-29 StartY=-11.5 StartZ=0 EndX=-29 EndY=11.5 EndZ=0
    g8: Circle [constr] CenterX=-29 CenterY=11.5 CenterZ=0 NormalX=0 NormalY=0 NormalZ=1 AngleXU=0 Radius=1.375
    g9: Circle [constr] CenterX=29 CenterY=11.5 CenterZ=0 NormalX=0 NormalY=0 NormalZ=1 AngleXU=0 Radius=1.375
    g10: Circle [constr] CenterX=29 CenterY=-11.5 CenterZ=0 NormalX=0 NormalY=0 NormalZ=1 AngleXU=0 Radius=1.375
    g11: Circle [constr] CenterX=-29 CenterY=-11.5 CenterZ=0 NormalX=0 NormalY=0 NormalZ=1 AngleXU=0 Radius=1.375
    g12: LineSegment [constr] StartX=-29.5 StartY=12 StartZ=0 EndX=29.5 EndY=12 EndZ=0
    g13: LineSegment [constr] StartX=29.5 StartY=12 StartZ=0 EndX=29.5 EndY=-12 EndZ=0
    g14: LineSegment [constr] StartX=29.5 StartY=-12 StartZ=0 EndX=-29.5 EndY=-12 EndZ=0
    g15: LineSegment [constr] StartX=-29.5 StartY=-12 StartZ=0 EndX=-29.5 EndY=12 EndZ=0
    g16: ArcOfCircle [constr] CenterX=-29.5 CenterY=12 CenterZ=0 NormalX=0 NormalY=0 NormalZ=1 AngleXU=0 Radius=3 StartAngle=1.5708 EndAngle=3.14159
    g17: ArcOfCircle [constr] CenterX=29.5 CenterY=12 CenterZ=0 NormalX=0 NormalY=0 NormalZ=1 AngleXU=0 Radius=3 StartAngle=3.6972e-08 EndAngle=1.5708
    g18: ArcOfCircle [constr] CenterX=29.5 CenterY=-12 CenterZ=0 NormalX=0 NormalY=0 NormalZ=1 AngleXU=0 Radius=3 StartAngle=4.71239 EndAngle=6.28319
    g19: ArcOfCircle [constr] CenterX=-29.5 CenterY=-12 CenterZ=0 NormalX=0 NormalY=0 NormalZ=1 AngleXU=0 Radius=3 StartAngle=3.14159 EndAngle=4.71239
    g20: LineSegment [constr] StartX=-29.5 StartY=15 StartZ=0 EndX=29.5 EndY=15 EndZ=0
    g21: LineSegment [constr] StartX=32.5 StartY=12 StartZ=0 EndX=32.5 EndY=-12 EndZ=0
    g22: LineSegment [constr] StartX=29.5 StartY=-15 StartZ=0 EndX=-29.5 EndY=-15 EndZ=0
    g23: LineSegment [constr] StartX=-32.5 StartY=-12 StartZ=0 EndX=-32.5 EndY=12 EndZ=0
    g24: ArcOfCircle [constr] CenterX=-29.5 CenterY=12 CenterZ=0 NormalX=0 NormalY=0 NormalZ=1 AngleXU=0 Radius=3.3 StartAngle=1.5708 EndAngle=3.14159
    g25: ArcOfCircle [constr] CenterX=29.5 CenterY=12 CenterZ=0 NormalX=0 NormalY=0 NormalZ=1 AngleXU=0 Radius=3.3 StartAngle=-4.27e-10 EndAngle=1.5708
    g26: ArcOfCircle [constr] CenterX=29.5 CenterY=-12 CenterZ=0 NormalX=0 NormalY=0 NormalZ=1 AngleXU=0 Radius=3.3 StartAngle=4.71239 EndAngle=6.28319
    g27: ArcOfCircle [constr] CenterX=-29.5 CenterY=-12 CenterZ=0 NormalX=0 NormalY=0 NormalZ=1 AngleXU=0 Radius=3.3 StartAngle=3.14159 EndAngle=4.71239
    g28: LineSegment [constr] StartX=-32.8 StartY=12 StartZ=0 EndX=-32.8 EndY=-12 EndZ=0
    g29: LineSegment [constr] StartX=-29.5 StartY=15.3 StartZ=0 EndX=29.5 EndY=15.3 EndZ=0
    g30: LineSegment [constr] StartX=32.8 StartY=12 StartZ=0 EndX=32.8 EndY=-12 EndZ=0
    g31: LineSegment [constr] StartX=29.5 StartY=-15.3 StartZ=0 EndX=-29.5 EndY=-15.3 EndZ=0
    g32: LineSegment [constr] StartX=-34.8 StartY=17.3 StartZ=0 EndX=34.8 EndY=17.3 EndZ=0
    g33: LineSegment [constr] StartX=34.8 StartY=17.3 StartZ=0 EndX=34.8 EndY=-17.3 EndZ=0
    g34: LineSegment [constr] StartX=34.8 StartY=-17.3 StartZ=0 EndX=-34.8 EndY=-17.3 EndZ=0
    g35: LineSegment [constr] StartX=-34.8 StartY=-17.3 StartZ=0 EndX=-34.8 EndY=17.3 EndZ=0
    g36: Circle [constr] CenterX=34.8 CenterY=17.3 CenterZ=0 NormalX=0 NormalY=0 NormalZ=1 AngleXU=0 Radius=5
    g37: Circle [constr] CenterX=34.8 CenterY=-17.3 CenterZ=0 NormalX=0 NormalY=0 NormalZ=1 AngleXU=0 Radius=5
    g38: Circle [constr] CenterX=-34.8 CenterY=-17.3 CenterZ=0 NormalX=0 NormalY=0 NormalZ=1 AngleXU=0 Radius=5
    g39: Circle [constr] CenterX=-34.8 CenterY=17.3 CenterZ=0 NormalX=0 NormalY=0 NormalZ=1 AngleXU=0 Radius=5
    g40: Circle [constr] CenterX=27.3838 CenterY=20.3 CenterZ=0 NormalX=0 NormalY=0 NormalZ=1 AngleXU=0 Radius=3
    g41: Circle [constr] CenterX=-27.3838 CenterY=20.3 CenterZ=0 NormalX=0 NormalY=0 NormalZ=1 AngleXU=0 Radius=3
    g42: Circle [constr] CenterX=-37.8 CenterY=9.8838 CenterZ=0 NormalX=0 NormalY=0 NormalZ=1 AngleXU=0 Radius=3
    g43: Circle [constr] CenterX=-37.8 CenterY=-9.8838 CenterZ=0 NormalX=0 NormalY=0 NormalZ=1 AngleXU=0 Radius=3
    g44: Circle [constr] CenterX=-27.3838 CenterY=-20.3 CenterZ=0 NormalX=0 NormalY=0 NormalZ=1 AngleXU=0 Radius=3
    g45: Circle [constr] CenterX=27.3838 CenterY=-20.3 CenterZ=0 NormalX=0 NormalY=0 NormalZ=1 AngleXU=0 Radius=3
    g46: Circle [constr] CenterX=37.8 CenterY=-9.8838 CenterZ=0 NormalX=0 NormalY=0 NormalZ=1 AngleXU=0 Radius=3
    g47: Circle [constr] CenterX=37.8 CenterY=9.8838 CenterZ=0 NormalX=0 NormalY=0 NormalZ=1 AngleXU=0 Radius=3
    g48: ArcOfCircle [constr] CenterX=34.8 CenterY=17.3 CenterZ=0 NormalX=0 NormalY=0 NormalZ=1 AngleXU=0 Radius=5 StartAngle=5.09679 EndAngle=9.04038
    g49: ArcOfCircle [constr] CenterX=27.3838 CenterY=20.3 CenterZ=0 NormalX=0 NormalY=0 NormalZ=1 AngleXU=0 Radius=3 StartAngle=4.71239 EndAngle=5.89879
    g50: ArcOfCircle [constr] CenterX=37.8 CenterY=9.8838 CenterZ=0 NormalX=0 NormalY=0 NormalZ=1 AngleXU=0 Radius=3 StartAngle=1.95519 EndAngle=3.14159
    g51: ArcOfCircle [constr] CenterX=37.8 CenterY=-9.8838 CenterZ=0 NormalX=0 NormalY=0 NormalZ=1 AngleXU=0 Radius=3 StartAngle=3.14159 EndAngle=4.32799
    g52: ArcOfCircle [constr] CenterX=34.8 CenterY=-17.3 CenterZ=0 NormalX=0 NormalY=0 NormalZ=1 AngleXU=0 Radius=5 StartAngle=3.52599 EndAngle=7.46958
    g53: ArcOfCircle [constr] CenterX=27.3838 CenterY=-20.3 CenterZ=0 NormalX=0 NormalY=0 NormalZ=1 AngleXU=0 Radius=3 StartAngle=0.384397 EndAngle=1.5708
    g54: ArcOfCircle [constr] CenterX=-27.3838 CenterY=-20.3 CenterZ=0 NormalX=0 NormalY=0 NormalZ=1 AngleXU=0 Radius=3 StartAngle=1.5708 EndAngle=2.7572
    g55: ArcOfCircle [constr] CenterX=-34.8 CenterY=-17.3 CenterZ=0 NormalX=0 NormalY=0 NormalZ=1 AngleXU=0 Radius=5 StartAngle=1.95519 EndAngle=5.89879
    g56: ArcOfCircle [constr] CenterX=-37.8 CenterY=-9.8838 CenterZ=0 NormalX=0 NormalY=0 NormalZ=1 AngleXU=0 Radius=3 StartAngle=5.09678 EndAngle=6.28319
    g57: ArcOfCircle [constr] CenterX=-37.8 CenterY=9.8838 CenterZ=0 NormalX=0 NormalY=0 NormalZ=1 AngleXU=0 Radius=3 StartAngle=4.4909e-08 EndAngle=1.1864
    g58: ArcOfCircle [constr] CenterX=-34.8 CenterY=17.3 CenterZ=0 NormalX=0 NormalY=0 NormalZ=1 AngleXU=0 Radius=5 StartAngle=0.384397 EndAngle=4.32799
    g59: ArcOfCircle [constr] CenterX=-27.3838 CenterY=20.3 CenterZ=0 NormalX=0 NormalY=0 NormalZ=1 AngleXU=0 Radius=3 StartAngle=3.52599 EndAngle=4.71239
    g60: LineSegment [constr] StartX=-27.3838 StartY=17.3 StartZ=0 EndX=27.3838 EndY=17.3 EndZ=0
    g61: LineSegment [constr] StartX=34.8 StartY=9.8838 StartZ=0 EndX=34.8 EndY=-9.8838 EndZ=0
    g62: LineSegment [constr] StartX=27.3838 StartY=-17.3 StartZ=0 EndX=-27.3838 EndY=-17.3 EndZ=0
    g63: LineSegment [constr] StartX=-34.8 StartY=-9.8838 StartZ=0 EndX=-34.8 EndY=9.8838 EndZ=0
    g64: ArcOfCircle CenterX=29 CenterY=11.5 CenterZ=0 NormalX=0 NormalY=0 NormalZ=1 AngleXU=0 Radius=3 StartAngle=3.14352 EndAngle=4.71046
    g65: ArcOfCircle CenterX=29.5 CenterY=12 CenterZ=0 NormalX=0 NormalY=0 NormalZ=1 AngleXU=0 Radius=3.3 StartAngle=2.17631e-07 EndAngle=1.5708
    g66: LineSegment StartX=26 StartY=15.3 StartZ=0 EndX=29.5 EndY=15.3 EndZ=0
    g67: LineSegment StartX=32.8 StartY=12 StartZ=0 EndX=32.8 EndY=8.50001 EndZ=0
    g68: LineSegment StartX=26 StartY=15.3 StartZ=0 EndX=26 EndY=11.4942 EndZ=0
    g69: LineSegment StartX=28.9942 StartY=8.50001 StartZ=0 EndX=32.8 EndY=8.50001 EndZ=0
    g70: LineSegment [constr] StartX=-43.6068 StartY=0 StartZ=0 EndX=51.9839 EndY=0 EndZ=0
    g71: LineSegment [constr] StartX=0 StartY=-19.8111 StartZ=0 EndX=0 EndY=22.459 EndZ=0
    g72: LineSegment StartX=26 StartY=-15.3 StartZ=0 EndX=26 EndY=-11.4942 EndZ=0
    g73: ArcOfCircle CenterX=29 CenterY=-11.5 CenterZ=0 NormalX=0 NormalY=0 NormalZ=1 AngleXU=0 Radius=3 StartAngle=1.57273 EndAngle=3.13966
    g74: LineSegment StartX=28.9942 StartY=-8.50001 StartZ=0 EndX=32.8 EndY=-8.50001 EndZ=0
    g75: LineSegment StartX=26 StartY=-15.3 StartZ=0 EndX=29.5 EndY=-15.3 EndZ=0
    g76: ArcOfCircle CenterX=29.5 CenterY=-12 CenterZ=0 NormalX=0 NormalY=0 NormalZ=1 AngleXU=0 Radius=3.3 StartAngle=4.71238 EndAngle=6.28319
    g77: LineSegment StartX=32.8 StartY=-12 StartZ=0 EndX=32.8 EndY=-8.50001 EndZ=0
    g78: LineSegment StartX=-28.9942 StartY=-8.50001 StartZ=0 EndX=-32.8 EndY=-8.50001 EndZ=0
    g79: LineSegment StartX=-32.8 StartY=-12 StartZ=0 EndX=-32.8 EndY=-8.50001 EndZ=0
    g80: ArcOfCircle CenterX=-29.5 CenterY=-12 CenterZ=0 NormalX=0 NormalY=0 NormalZ=1 AngleXU=0 Radius=3.3 StartAngle=3.14159 EndAngle=4.71239
    g81: LineSegment StartX=-26 StartY=-15.3 StartZ=0 EndX=-29.5 EndY=-15.3 EndZ=0
    g82: LineSegment StartX=-26 StartY=-15.3 StartZ=0 EndX=-26 EndY=-11.4942 EndZ=0
    g83: ArcOfCircle CenterX=-29 CenterY=-11.5 CenterZ=0 NormalX=0 NormalY=0 NormalZ=1 AngleXU=0 Radius=3 StartAngle=0.00192871 EndAngle=1.56886
    g84: LineSegment StartX=-28.9942 StartY=8.50001 StartZ=0 EndX=-32.8 EndY=8.50001 EndZ=0
    g85: LineSegment StartX=-32.8 StartY=12 StartZ=0 EndX=-32.8 EndY=8.50001 EndZ=0
    g86: ArcOfCircle CenterX=-29.5 CenterY=12 CenterZ=0 NormalX=0 NormalY=0 NormalZ=1 AngleXU=0 Radius=3.3 StartAngle=1.57079 EndAngle=3.14159
    g87: LineSegment StartX=-26 StartY=15.3 StartZ=0 EndX=-29.5 EndY=15.3 EndZ=0
    g88: LineSegment StartX=-26 StartY=15.3 StartZ=0 EndX=-26 EndY=11.4942 EndZ=0
    g89: ArcOfCircle CenterX=-29 CenterY=11.5 CenterZ=0 NormalX=0 NormalY=0 NormalZ=1 AngleXU=0 Radius=3 StartAngle=4.71432 EndAngle=6.28126
    g90: Circle CenterX=29 CenterY=11.5 CenterZ=0 NormalX=0 NormalY=0 NormalZ=1 AngleXU=0 Radius=0.5
    g91: Circle CenterX=-29 CenterY=-11.5 CenterZ=0 NormalX=0 NormalY=0 NormalZ=1 AngleXU=0 Radius=0.5
  constraints (241):
    c: Coincident(g0,g1)
    c: Coincident(g1,g2)
    c: Coincident(g2,g3)
    c: Coincident(g3,g0)
    c: Horizontal(g0)
    c: Horizontal(g2)
    c: Vertical(g1)
    c: Vertical(g3)
    c: DistanceX(g0,g0) = 65
    c: DistanceY(g1,g1) = 30
    c: Symmetric(g0,g0,g-2)
    c: Symmetric(g0,g1,g-1)
    c: Coincident(g4,g5)
    c: Coincident(g5,g6)
    c: Coincident(g6,g7)
    c: Coincident(g7,g4)
    c: Horizontal(g4)
    c: Horizontal(g6)
    c: Vertical(g5)
    c: Vertical(g7)
    c: DistanceX(g4,g4) = 58
    c: DistanceY(g5,g5) = 23
    c: Symmetric(g4,g5,g-1)
    c: Symmetric(g4,g4,g-2)
    c: Coincident(g8,g4)
    c: Coincident(g9,g4)
    c: Coincident(g10,g5)
    c: Coincident(g11,g6)
    c: Radius(g11) = 1.375
    c: Radius(g8) = 1.375
    c: Radius(g9) = 1.375
    c: Radius(g10) = 1.375
    c: Coincident(g12,g13)
    c: Coincident(g13,g14)
    c: Coincident(g14,g15)
    c: Coincident(g15,g12)
    c: Horizontal(g12)
    c: Horizontal(g14)
    c: Vertical(g13)
    c: Vertical(g15)
    c: DistanceX(g4,g12) = 0.5
    c: DistanceY(g4,g12) = 0.5
    c: DistanceY(g13,g5) = 0.5
    c: DistanceX(g14,g6) = 0.5
    c: Coincident(g16,g12)
    c: Radius(g16) = 3
    c: Coincident(g17,g12)
    c: Radius(g17) = 3
    c: Coincident(g18,g13)
    c: Radius(g18) = 3
    c: Coincident(g19,g14)
    c: Radius(g19) = 3
    c: PointOnObject(g16,g0)
    c: PointOnObject(g17,g1)
    c: PointOnObject(g18,g2)
    c: PointOnObject(g19,g3)
    c: Coincident(g20,g16)
    c: Horizontal(g20)
    c: Coincident(g20,g17)
    c: Coincident(g21,g17)
    c: Vertical(g21)
    c: Coincident(g18,g21)
    c: Coincident(g22,g18)
    c: Horizontal(g22)
    c: Coincident(g19,g22)
    c: Coincident(g23,g19)
    c: Vertical(g23)
    c: Coincident(g23,g16)
    c: Coincident(g24,g12)
    c: Radius(g24) = 3.3
    c: Coincident(g25,g12)
    c: Radius(g25) = 3.3
    c: Coincident(g26,g13)
    c: Radius(g26) = 3.3
    c: Coincident(g27,g14)
    c: Radius(g27) = 3.3
    c: Vertical(g28)
    c: DistanceX(g28,g2) = 0.3
    c: Coincident(g27,g28)
    c: Coincident(g28,g24)
    c: Horizontal(g29)
    c: DistanceY(g0,g29) = 0.3
    c: Coincident(g24,g29)
    c: Coincident(g25,g29)
    c: Vertical(g30)
    c: DistanceX(g0,g30) = 0.3
    c: Coincident(g25,g30)
    c: Coincident(g30,g26)
    c: Horizontal(g31)
    c: DistanceY(g31,g1) = 0.3
    c: Coincident(g31,g26)
    c: Coincident(g31,g27)
    c: Coincident(g32,g33)
    c: Coincident(g33,g34)
    c: Coincident(g34,g35)
    c: Coincident(g35,g32)
    c: Horizontal(g32)
    c: Horizontal(g34)
    c: Vertical(g33)
    c: Vertical(g35)
    c: DistanceY(g25,g32) = 2
    c: DistanceX(g25,g32) = 2
    c: DistanceY(g33,g26) = 2
    c: DistanceX(g34,g27) = 2
    c: Coincident(g36,g32)
    c: Coincident(g37,g33)
    c: Coincident(g38,g34)
    c: Coincident(g39,g32)
    c: Radius(g39) = 5
    c: Radius(g38) = 5
    c: Radius(g37) = 5
    c: Radius(g36) = 5
    c: Radius(g40) = 3
    c: Tangent(g40,g36)
    c: Tangent(g40,g32)
    c: Tangent(g47,g36)
    c: Radius(g47) = 3
    c: Tangent(g47,g33)
    c: Radius(g46) = 3
    c: Tangent(g46,g37)
    c: Tangent(g46,g33)
    c: Radius(g45) = 3
    c: Tangent(g45,g37)
    c: Tangent(g45,g34)
    c: Radius(g44) = 3
    c: Tangent(g44,g34)
    c: Tangent(g44,g38)
    c: Radius(g43) = 3
    c: Tangent(g43,g38)
    c: Tangent(g43,g35)
    c: Radius(g42) = 3
    c: Tangent(g42,g35)
    c: Tangent(g42,g39)
    c: Radius(g41) = 3
    c: Tangent(g41,g32)
    c: Tangent(g41,g39)
    c: Coincident(g48,g32)
    c: PointOnObject(g48,g36)
    c: Coincident(g49,g40)
    c: PointOnObject(g49,g40)
    c: Coincident(g50,g47)
    c: PointOnObject(g50,g47)
    c: Coincident(g51,g46)
    c: PointOnObject(g51,g46)
    c: Coincident(g52,g33)
    c: PointOnObject(g52,g37)
    c: Coincident(g53,g45)
    c: PointOnObject(g53,g45)
    c: Coincident(g54,g44)
    c: PointOnObject(g54,g44)
    c: Coincident(g55,g34)
    c: PointOnObject(g55,g38)
    c: Coincident(g56,g43)
    c: PointOnObject(g56,g43)
    c: Coincident(g57,g42)
    c: PointOnObject(g57,g42)
    c: Coincident(g58,g32)
    c: PointOnObject(g58,g39)
    c: Coincident(g59,g41)
    c: PointOnObject(g59,g41)
    c: Coincident(g49,g48)
    c: Coincident(g48,g50)
    c: Coincident(g51,g52)
    c: Coincident(g52,g53)
    c: Coincident(g54,g55)
    c: Coincident(g55,g56)
    c: Coincident(g57,g58)
    c: Coincident(g58,g59)
    c: PointOnObject(g60,g32)
    c: Horizontal(g60)
    c: PointOnObject(g61,g33)
    c: Vertical(g61)
    c: PointOnObject(g62,g34)
    c: Horizontal(g62)
    c: PointOnObject(g63,g35)
    c: Vertical(g63)
    c: Coincident(g59,g60)
    c: Coincident(g60,g49)
    c: Coincident(g50,g61)
    c: Coincident(g61,g51)
    c: Coincident(g53,g62)
    c: Coincident(g54,g62)
    c: Coincident(g56,g63)
    c: Coincident(g57,g63)
    c: Coincident(g64,g4)
    c: Radius(g64) = 3
    c: Coincident(g65,g12)
    c: PointOnObject(g66,g29)
    c: Horizontal(g66)
    c: Coincident(g65,g66)
    c: PointOnObject(g65,g25)
    c: PointOnObject(g67,g30)
    c: Vertical(g67)
    c: Coincident(g67,g65)
    c: Vertical(g68)
    c: Coincident(g68,g64)
    c: Coincident(g68,g66)
    c: Horizontal(g69)
    c: Coincident(g64,g69)
    c: Coincident(g67,g69)
    c: PointOnObject(g70,g-1)
    c: Horizontal(g70)
    c: PointOnObject(g71,g-2)
    c: Vertical(g71)
    c: Radius(g73) = 3
    c: Horizontal(g75)
    c: Coincident(g76,g75)
    c: Vertical(g77)
    c: Coincident(g77,g76)
    c: Vertical(g72)
    c: Coincident(g72,g73)
    c: Coincident(g72,g75)
    c: Horizontal(g74)
    c: Coincident(g73,g74)
    c: Coincident(g77,g74)
    c: Radius(g89) = 3
    c: Horizontal(g87)
    c: Coincident(g86,g87)
    c: Vertical(g85)
    c: Coincident(g85,g86)
    c: Vertical(g88)
    c: Coincident(g88,g89)
    c: Coincident(g88,g87)
    c: Horizontal(g84)
    c: Coincident(g89,g84)
    c: Coincident(g85,g84)
    c: Radius(g83) = 3
    c: Horizontal(g81)
    c: Coincident(g80,g81)
    c: Vertical(g79)
    c: Coincident(g79,g80)
    c: Vertical(g82)
    c: Coincident(g82,g83)
    c: Coincident(g82,g81)
    c: Horizontal(g78)
    c: Coincident(g83,g78)
    c: Coincident(g79,g78)
    c: Coincident(g90,g4)
    c: Radius(g90) = 0.5
    c: Coincident(g91,g6)
    c: Radius(g91) = 0.5
FEATURE [PartDesign::Pad] Pad001
  BaseFeature = -> Pocket
  Length = 2
  Length2 = 100
  Profile = -> Sketch003
  Type = 0
FEATURE [Sketcher::SketchObject] Sketch004
  MapMode = 5
  Placement = pos=(0,0,8.5) rot=(0,0,1;0rad)
  Support = -> [Pad001]
  expr: Constraints[133] = Sketch001.Constraints[133]
  expr: Constraints[130] = Sketch001.Constraints[130]
  expr: Constraints[112] = Sketch001.Constraints[112]
  expr: Constraints[127] = Sketch001.Constraints[127]
  expr: Constraints[124] = Sketch001.Constraints[124]
  expr: Constraints[110] = Sketch001.Constraints[110]
  expr: Constraints[51] = Sketch001.Constraints[51]
  expr: Constraints[100] = Sketch001.Constraints[100]
  expr: Constraints[77] = Sketch001.Constraints[77]
  expr: Constraints[89] = Sketch001.Constraints[89]
  expr: Constraints[118] = Sketch001.Constraints[118]
  expr: Constraints[85] = Sketch001.Constraints[85]
  expr: Constraints[103] = Sketch001.Constraints[103]
  expr: Constraints[111] = Sketch001.Constraints[111]
  expr: Constraints[71] = Sketch001.Constraints[71]
  expr: Constraints[49] = Sketch001.Constraints[49]
  expr: Constraints[102] = Sketch001.Constraints[102]
  expr: Constraints[69] = Sketch001.Constraints[69]
  expr: Constraints[47] = Sketch001.Constraints[47]
  expr: Constraints[73] = Sketch001.Constraints[73]
  expr: Constraints[75] = Sketch001.Constraints[75]
  expr: Constraints[31] = Sketch001.Constraints[31]
  expr: Constraints[116] = Sketch001.Constraints[116]
  expr: Constraints[40] = Sketch001.Constraints[40]
  expr: Constraints[30] = Sketch001.Constraints[30]
  expr: Constraints[29] = Sketch001.Constraints[29]
  expr: Constraints[121] = Sketch001.Constraints[121]
  expr: Constraints[28] = Sketch001.Constraints[28]
  expr: Constraints[21] = Sketch001.Constraints[21]
  expr: Constraints[20] = Sketch001.Constraints[20]
  expr: Constraints[45] = Sketch001.Constraints[45]
  expr: Constraints[108] = Sketch001.Constraints[108]
  expr: Constraints[43] = Sketch001.Constraints[43]
  expr: Constraints[42] = Sketch001.Constraints[42]
  expr: Constraints[101] = Sketch001.Constraints[101]
  expr: Constraints[109] = Sketch001.Constraints[109]
  expr: Constraints[41] = Sketch001.Constraints[41]
  expr: Constraints[9] = Sketch001.Constraints[9]
  expr: Constraints[81] = Sketch001.Constraints[81]
  expr: Constraints[8] = Sketch001.Constraints[8]
  sketch-geometry (68):
    g0: LineSegment [constr] StartX=-32.5 StartY=15 StartZ=0 EndX=32.5 EndY=15 EndZ=0
    g1: LineSegment [constr] StartX=32.5 StartY=15 StartZ=0 EndX=32.5 EndY=-15 EndZ=0
    g2: LineSegment [constr] StartX=32.5 StartY=-15 StartZ=0 EndX=-32.5 EndY=-15 EndZ=0
    g3: LineSegment [constr] StartX=-32.5 StartY=-15 StartZ=0 EndX=-32.5 EndY=15 EndZ=0
    g4: LineSegment [constr] StartX=-29 StartY=11.5 StartZ=0 EndX=29 EndY=11.5 EndZ=0
    g5: LineSegment [constr] StartX=29 StartY=11.5 StartZ=0 EndX=29 EndY=-11.5 EndZ=0
    g6: LineSegment [constr] StartX=29 StartY=-11.5 StartZ=0 EndX=-29 EndY=-11.5 EndZ=0
    g7: LineSegment [constr] StartX=-29 StartY=-11.5 StartZ=0 EndX=-29 EndY=11.5 EndZ=0
    g8: Circle [constr] CenterX=-29 CenterY=11.5 CenterZ=0 NormalX=0 NormalY=0 NormalZ=1 AngleXU=0 Radius=1.375
    g9: Circle [constr] CenterX=29 CenterY=11.5 CenterZ=0 NormalX=0 NormalY=0 NormalZ=1 AngleXU=0 Radius=1.375
    g10: Circle [constr] CenterX=29 CenterY=-11.5 CenterZ=0 NormalX=0 NormalY=0 NormalZ=1 AngleXU=0 Radius=1.375
    g11: Circle [constr] CenterX=-29 CenterY=-11.5 CenterZ=0 NormalX=0 NormalY=0 NormalZ=1 AngleXU=0 Radius=1.375
    g12: LineSegment [constr] StartX=-29.5 StartY=12 StartZ=0 EndX=29.5 EndY=12 EndZ=0
    g13: LineSegment [constr] StartX=29.5 StartY=12 StartZ=0 EndX=29.5 EndY=-12 EndZ=0
    g14: LineSegment [constr] StartX=29.5 StartY=-12 StartZ=0 EndX=-29.5 EndY=-12 EndZ=0
    g15: LineSegment [constr] StartX=-29.5 StartY=-12 StartZ=0 EndX=-29.5 EndY=12 EndZ=0
    g16: ArcOfCircle [constr] CenterX=-29.5 CenterY=12 CenterZ=0 NormalX=0 NormalY=0 NormalZ=1 AngleXU=0 Radius=3 StartAngle=1.5708 EndAngle=3.14159
    g17: ArcOfCircle [constr] CenterX=29.5 CenterY=12 CenterZ=0 NormalX=0 NormalY=0 NormalZ=1 AngleXU=0 Radius=3 StartAngle=2.8425e-08 EndAngle=1.5708
    g18: ArcOfCircle [constr] CenterX=29.5 CenterY=-12 CenterZ=0 NormalX=0 NormalY=0 NormalZ=1 AngleXU=0 Radius=3 StartAngle=4.71239 EndAngle=6.28319
    g19: ArcOfCircle [constr] CenterX=-29.5 CenterY=-12 CenterZ=0 NormalX=0 NormalY=0 NormalZ=1 AngleXU=0 Radius=3 StartAngle=3.14159 EndAngle=4.71239
    g20: LineSegment [constr] StartX=-29.5 StartY=15 StartZ=0 EndX=29.5 EndY=15 EndZ=0
    g21: LineSegment [constr] StartX=32.5 StartY=12 StartZ=0 EndX=32.5 EndY=-12 EndZ=0
    g22: LineSegment [constr] StartX=29.5 StartY=-15 StartZ=0 EndX=-29.5 EndY=-15 EndZ=0
    g23: LineSegment [constr] StartX=-32.5 StartY=-12 StartZ=0 EndX=-32.5 EndY=12 EndZ=0
    g24: ArcOfCircle [constr] CenterX=-29.5 CenterY=12 CenterZ=0 NormalX=0 NormalY=0 NormalZ=1 AngleXU=0 Radius=3.3 StartAngle=1.5708 EndAngle=3.14159
    g25: ArcOfCircle [constr] CenterX=29.5 CenterY=12 CenterZ=0 NormalX=0 NormalY=0 NormalZ=1 AngleXU=0 Radius=3.3 StartAngle=-2.2e-10 EndAngle=1.5708
    g26: ArcOfCircle [constr] CenterX=29.5 CenterY=-12 CenterZ=0 NormalX=0 NormalY=0 NormalZ=1 AngleXU=0 Radius=3.3 StartAngle=4.71239 EndAngle=6.28319
    g27: ArcOfCircle [constr] CenterX=-29.5 CenterY=-12 CenterZ=0 NormalX=0 NormalY=0 NormalZ=1 AngleXU=0 Radius=3.3 StartAngle=3.14159 EndAngle=4.71239
    g28: LineSegment [constr] StartX=-32.8 StartY=12 StartZ=0 EndX=-32.8 EndY=-12 EndZ=0
    g29: LineSegment [constr] StartX=-29.5 StartY=15.3 StartZ=0 EndX=29.5 EndY=15.3 EndZ=0
    g30: LineSegment [constr] StartX=32.8 StartY=12 StartZ=0 EndX=32.8 EndY=-12 EndZ=0
    g31: LineSegment [constr] StartX=29.5 StartY=-15.3 StartZ=0 EndX=-29.5 EndY=-15.3 EndZ=0
    g32: LineSegment [constr] StartX=-34.8 StartY=17.3 StartZ=0 EndX=34.8 EndY=17.3 EndZ=0
    g33: LineSegment [constr] StartX=34.8 StartY=17.3 StartZ=0 EndX=34.8 EndY=-17.3 EndZ=0
    g34: LineSegment [constr] StartX=34.8 StartY=-17.3 StartZ=0 EndX=-34.8 EndY=-17.3 EndZ=0
    g35: LineSegment [constr] StartX=-34.8 StartY=-17.3 StartZ=0 EndX=-34.8 EndY=17.3 EndZ=0
    g36: Circle [constr] CenterX=34.8 CenterY=17.3 CenterZ=0 NormalX=0 NormalY=0 NormalZ=1 AngleXU=0 Radius=5
    g37: Circle [constr] CenterX=34.8 CenterY=-17.3 CenterZ=0 NormalX=0 NormalY=0 NormalZ=1 AngleXU=0 Radius=5
    g38: Circle [constr] CenterX=-34.8 CenterY=-17.3 CenterZ=0 NormalX=0 NormalY=0 NormalZ=1 AngleXU=0 Radius=5
    g39: Circle [constr] CenterX=-34.8 CenterY=17.3 CenterZ=0 NormalX=0 NormalY=0 NormalZ=1 AngleXU=0 Radius=5
    g40: Circle [constr] CenterX=27.3838 CenterY=20.3 CenterZ=0 NormalX=0 NormalY=0 NormalZ=1 AngleXU=0 Radius=3
    g41: Circle [constr] CenterX=-27.3838 CenterY=20.3 CenterZ=0 NormalX=0 NormalY=0 NormalZ=1 AngleXU=0 Radius=3
    g42: Circle [constr] CenterX=-37.8 CenterY=9.8838 CenterZ=0 NormalX=0 NormalY=0 NormalZ=1 AngleXU=0 Radius=3
    g43: Circle [constr] CenterX=-37.8 CenterY=-9.8838 CenterZ=0 NormalX=0 NormalY=0 NormalZ=1 AngleXU=0 Radius=3
    g44: Circle [constr] CenterX=-27.3838 CenterY=-20.3 CenterZ=0 NormalX=0 NormalY=0 NormalZ=1 AngleXU=0 Radius=3
    g45: Circle [constr] CenterX=27.3838 CenterY=-20.3 CenterZ=0 NormalX=0 NormalY=0 NormalZ=1 AngleXU=0 Radius=3
    g46: Circle [constr] CenterX=37.8 CenterY=-9.8838 CenterZ=0 NormalX=0 NormalY=0 NormalZ=1 AngleXU=0 Radius=3
    g47: Circle [constr] CenterX=37.8 CenterY=9.8838 CenterZ=0 NormalX=0 NormalY=0 NormalZ=1 AngleXU=0 Radius=3
    g48: ArcOfCircle [constr] CenterX=34.8 CenterY=17.3 CenterZ=0 NormalX=0 NormalY=0 NormalZ=1 AngleXU=0 Radius=5 StartAngle=5.09679 EndAngle=9.04038
    g49: ArcOfCircle [constr] CenterX=27.3838 CenterY=20.3 CenterZ=0 NormalX=0 NormalY=0 NormalZ=1 AngleXU=0 Radius=3 StartAngle=4.71239 EndAngle=5.89879
    g50: ArcOfCircle [constr] CenterX=37.8 CenterY=9.8838 CenterZ=0 NormalX=0 NormalY=0 NormalZ=1 AngleXU=0 Radius=3 StartAngle=1.95519 EndAngle=3.14159
    g51: ArcOfCircle [constr] CenterX=37.8 CenterY=-9.8838 CenterZ=0 NormalX=0 NormalY=0 NormalZ=1 AngleXU=0 Radius=3 StartAngle=3.14159 EndAngle=4.32799
    g52: ArcOfCircle [constr] CenterX=34.8 CenterY=-17.3 CenterZ=0 NormalX=0 NormalY=0 NormalZ=1 AngleXU=0 Radius=5 StartAngle=3.52599 EndAngle=7.46958
    g53: ArcOfCircle [constr] CenterX=27.3838 CenterY=-20.3 CenterZ=0 NormalX=0 NormalY=0 NormalZ=1 AngleXU=0 Radius=3 StartAngle=0.384397 EndAngle=1.5708
    g54: ArcOfCircle [constr] CenterX=-27.3838 CenterY=-20.3 CenterZ=0 NormalX=0 NormalY=0 NormalZ=1 AngleXU=0 Radius=3 StartAngle=1.5708 EndAngle=2.7572
    g55: ArcOfCircle [constr] CenterX=-34.8 CenterY=-17.3 CenterZ=0 NormalX=0 NormalY=0 NormalZ=1 AngleXU=0 Radius=5 StartAngle=1.95519 EndAngle=5.89879
    g56: ArcOfCircle [constr] CenterX=-37.8 CenterY=-9.8838 CenterZ=0 NormalX=0 NormalY=0 NormalZ=1 AngleXU=0 Radius=3 StartAngle=5.09679 EndAngle=6.28319
    g57: ArcOfCircle [constr] CenterX=-37.8 CenterY=9.8838 CenterZ=0 NormalX=0 NormalY=0 NormalZ=1 AngleXU=0 Radius=3 StartAngle=6.28319 EndAngle=7.46958
    g58: ArcOfCircle [constr] CenterX=-34.8 CenterY=17.3 CenterZ=0 NormalX=0 NormalY=0 NormalZ=1 AngleXU=0 Radius=5 StartAngle=0.384397 EndAngle=4.32799
    g59: ArcOfCircle [constr] CenterX=-27.3838 CenterY=20.3 CenterZ=0 NormalX=0 NormalY=0 NormalZ=1 AngleXU=0 Radius=3 StartAngle=3.52599 EndAngle=4.71239
    g60: LineSegment [constr] StartX=-27.3838 StartY=17.3 StartZ=0 EndX=27.3838 EndY=17.3 EndZ=0
    g61: LineSegment [constr] StartX=34.8 StartY=9.8838 StartZ=0 EndX=34.8 EndY=-9.8838 EndZ=0
    g62: LineSegment [constr] StartX=27.3838 StartY=-17.3 StartZ=0 EndX=-27.3838 EndY=-17.3 EndZ=0
    g63: LineSegment [constr] StartX=-34.8 StartY=-9.8838 StartZ=0 EndX=-34.8 EndY=9.8838 EndZ=0
    g64: Circle CenterX=34.8 CenterY=17.3 CenterZ=0 NormalX=0 NormalY=0 NormalZ=1 AngleXU=0 Radius=3.2
    g65: Circle CenterX=34.8 CenterY=-17.3 CenterZ=0 NormalX=0 NormalY=0 NormalZ=1 AngleXU=0 Radius=3.2
    g66: Circle CenterX=-34.8 CenterY=-17.3 CenterZ=0 NormalX=0 NormalY=0 NormalZ=1 AngleXU=0 Radius=3.2
    g67: Circle CenterX=-34.8 CenterY=17.3 CenterZ=0 NormalX=0 NormalY=0 NormalZ=1 AngleXU=0 Radius=3.2
  constraints (192):
    c: Coincident(g0,g1)
    c: Coincident(g1,g2)
    c: Coincident(g2,g3)
    c: Coincident(g3,g0)
    c: Horizontal(g0)
    c: Horizontal(g2)
    c: Vertical(g1)
    c: Vertical(g3)
    c: DistanceX(g0,g0) = 65
    c: DistanceY(g1,g1) = 30
    c: Symmetric(g0,g0,g-2)
    c: Symmetric(g0,g1,g-1)
    c: Coincident(g4,g5)
    c: Coincident(g5,g6)
    c: Coincident(g6,g7)
    c: Coincident(g7,g4)
    c: Horizontal(g4)
    c: Horizontal(g6)
    c: Vertical(g5)
    c: Vertical(g7)
    c: DistanceX(g4,g4) = 58
    c: DistanceY(g5,g5) = 23
    c: Symmetric(g4,g5,g-1)
    c: Symmetric(g4,g4,g-2)
    c: Coincident(g8,g4)
    c: Coincident(g9,g4)
    c: Coincident(g10,g5)
    c: Coincident(g11,g6)
    c: Radius(g11) = 1.375
    c: Radius(g8) = 1.375
    c: Radius(g9) = 1.375
    c: Radius(g10) = 1.375
    c: Coincident(g12,g13)
    c: Coincident(g13,g14)
    c: Coincident(g14,g15)
    c: Coincident(g15,g12)
    c: Horizontal(g12)
    c: Horizontal(g14)
    c: Vertical(g13)
    c: Vertical(g15)
    c: DistanceX(g4,g12) = 0.5
    c: DistanceY(g4,g12) = 0.5
    c: DistanceY(g13,g5) = 0.5
    c: DistanceX(g14,g6) = 0.5
    c: Coincident(g16,g12)
    c: Radius(g16) = 3
    c: Coincident(g17,g12)
    c: Radius(g17) = 3
    c: Coincident(g18,g13)
    c: Radius(g18) = 3
    c: Coincident(g19,g14)
    c: Radius(g19) = 3
    c: PointOnObject(g16,g0)
    c: PointOnObject(g17,g1)
    c: PointOnObject(g18,g2)
    c: PointOnObject(g19,g3)
    c: Coincident(g20,g16)
    c: Horizontal(g20)
    c: Coincident(g20,g17)
    c: Coincident(g21,g17)
    c: Vertical(g21)
    c: Coincident(g18,g21)
    c: Coincident(g22,g18)
    c: Horizontal(g22)
    c: Coincident(g19,g22)
    c: Coincident(g23,g19)
    c: Vertical(g23)
    c: Coincident(g23,g16)
    c: Coincident(g24,g12)
    c: Radius(g24) = 3.3
    c: Coincident(g25,g12)
    c: Radius(g25) = 3.3
    c: Coincident(g26,g13)
    c: Radius(g26) = 3.3
    c: Coincident(g27,g14)
    c: Radius(g27) = 3.3
    c: Vertical(g28)
    c: DistanceX(g28,g2) = 0.3
    c: Coincident(g27,g28)
    c: Coincident(g28,g24)
    c: Horizontal(g29)
    c: DistanceY(g0,g29) = 0.3
    c: Coincident(g24,g29)
    c: Coincident(g25,g29)
    c: Vertical(g30)
    c: DistanceX(g0,g30) = 0.3
    c: Coincident(g25,g30)
    c: Coincident(g30,g26)
    c: Horizontal(g31)
    c: DistanceY(g31,g1) = 0.3
    c: Coincident(g31,g26)
    c: Coincident(g31,g27)
    c: Coincident(g32,g33)
    c: Coincident(g33,g34)
    c: Coincident(g34,g35)
    c: Coincident(g35,g32)
    c: Horizontal(g32)
    c: Horizontal(g34)
    c: Vertical(g33)
    c: Vertical(g35)
    c: DistanceY(g25,g32) = 2
    c: DistanceX(g25,g32) = 2
    c: DistanceY(g33,g26) = 2
    c: DistanceX(g34,g27) = 2
    c: Coincident(g36,g32)
    c: Coincident(g37,g33)
    c: Coincident(g38,g34)
    c: Coincident(g39,g32)
    c: Radius(g39) = 5
    c: Radius(g38) = 5
    c: Radius(g37) = 5
    c: Radius(g36) = 5
    c: Radius(g40) = 3
    c: Tangent(g40,g36)
    c: Tangent(g40,g32)
    c: Tangent(g47,g36)
    c: Radius(g47) = 3
    c: Tangent(g47,g33)
    c: Radius(g46) = 3
    c: Tangent(g46,g37)
    c: Tangent(g46,g33)
    c: Radius(g45) = 3
    c: Tangent(g45,g37)
    c: Tangent(g45,g34)
    c: Radius(g44) = 3
    c: Tangent(g44,g34)
    c: Tangent(g44,g38)
    c: Radius(g43) = 3
    c: Tangent(g43,g38)
    c: Tangent(g43,g35)
    c: Radius(g42) = 3
    c: Tangent(g42,g35)
    c: Tangent(g42,g39)
    c: Radius(g41) = 3
    c: Tangent(g41,g32)
    c: Tangent(g41,g39)
    c: Coincident(g48,g32)
    c: PointOnObject(g48,g36)
    c: Coincident(g49,g40)
    c: PointOnObject(g49,g40)
    c: Coincident(g50,g47)
    c: PointOnObject(g50,g47)
    c: Coincident(g51,g46)
    c: PointOnObject(g51,g46)
    c: Coincident(g52,g33)
    c: PointOnObject(g52,g37)
    c: Coincident(g53,g45)
    c: PointOnObject(g53,g45)
    c: Coincident(g54,g44)
    c: PointOnObject(g54,g44)
    c: Coincident(g55,g34)
    c: PointOnObject(g55,g38)
    c: Coincident(g56,g43)
    c: PointOnObject(g56,g43)
    c: Coincident(g57,g42)
    c: PointOnObject(g57,g42)
    c: Coincident(g58,g32)
    c: PointOnObject(g58,g39)
    c: Coincident(g59,g41)
    c: PointOnObject(g59,g41)
    c: Coincident(g49,g48)
    c: Coincident(g48,g50)
    c: Coincident(g51,g52)
    c: Coincident(g52,g53)
    c: Coincident(g54,g55)
    c: Coincident(g55,g56)
    c: Coincident(g57,g58)
    c: Coincident(g58,g59)
    c: PointOnObject(g60,g32)
    c: Horizontal(g60)
    c: PointOnObject(g61,g33)
    c: Vertical(g61)
    c: PointOnObject(g62,g34)
    c: Horizontal(g62)
    c: PointOnObject(g63,g35)
    c: Vertical(g63)
    c: Coincident(g59,g60)
    c: Coincident(g60,g49)
    c: Coincident(g50,g61)
    c: Coincident(g61,g51)
    c: Coincident(g53,g62)
    c: Coincident(g54,g62)
    c: Coincident(g56,g63)
    c: Coincident(g57,g63)
    c: Coincident(g64,g32)
    c: Coincident(g65,g33)
    c: Coincident(g66,g34)
    c: Coincident(g67,g32)
    c: Radius(g67) = 3.2
    c: Radius(g64) = 3.2
    c: Radius(g65) = 3.2
    c: Radius(g66) = 3.2
FEATURE [PartDesign::Pad] Pad002
  BaseFeature = -> Pad001
  Length = 2
  Length2 = 100
  Profile = -> Sketch004
  Type = 0
FEATURE [Sketcher::SketchObject] Sketch005
  MapMode = 5
  Placement = pos=(0,-17.3,-3.5) rot=(1,0,0;1.5708rad)
  sketch-geometry (22):
    g0: LineSegment StartX=-26.0242 StartY=12 StartZ=0 EndX=-14.2242 EndY=12 EndZ=0
    g1: LineSegment StartX=-14.2242 StartY=12 StartZ=0 EndX=-14.2242 EndY=9.7 EndZ=0
    g2: LineSegment StartX=-26.0242 StartY=9.7 StartZ=0 EndX=-26.0242 EndY=12 EndZ=0
    g3: LineSegment [constr] StartX=-20.1242 StartY=16.7174 StartZ=0 EndX=-20.1242 EndY=2.05389 EndZ=0
    g4: LineSegment [constr] StartX=-26 StartY=7.5 StartZ=0 EndX=23.454 EndY=7.5 EndZ=0
    g5: LineSegment StartX=-24.5941 StartY=8.5 StartZ=0 EndX=-15.6543 EndY=8.5 EndZ=0
    g6: LineSegment StartX=-26.0242 StartY=9.7 StartZ=0 EndX=-24.5941 EndY=8.5 EndZ=0
    g7: LineSegment StartX=-15.6543 StartY=8.5 StartZ=0 EndX=-14.2242 EndY=9.7 EndZ=0
    g8: LineSegment StartX=4.8858 StartY=12 StartZ=0 EndX=12.8858 EndY=12 EndZ=0
    g9: LineSegment StartX=12.8858 StartY=12 StartZ=0 EndX=12.8858 EndY=9.28 EndZ=0
    g10: LineSegment StartX=4.8858 StartY=9.28 StartZ=0 EndX=4.8858 EndY=12 EndZ=0
    g11: LineSegment [constr] StartX=8.8858 StartY=17.7004 StartZ=0 EndX=8.8858 EndY=3.91586 EndZ=0
    g12: LineSegment StartX=4.8858 StartY=9.28 StartZ=0 EndX=5.8858 EndY=8.28 EndZ=0
    g13: LineSegment StartX=11.8858 StartY=8.28 StartZ=0 EndX=12.8858 EndY=9.28 EndZ=0
    g14: LineSegment StartX=5.8858 StartY=8.28 StartZ=0 EndX=11.8858 EndY=8.28 EndZ=0
    g15: LineSegment StartX=17.5058 StartY=12 StartZ=0 EndX=25.5058 EndY=12 EndZ=0
    g16: LineSegment StartX=25.5058 StartY=12 StartZ=0 EndX=25.5058 EndY=9.28 EndZ=0
    g17: LineSegment StartX=17.5058 StartY=9.28 StartZ=0 EndX=17.5058 EndY=12 EndZ=0
    g18: LineSegment StartX=17.5058 StartY=9.28 StartZ=0 EndX=18.5058 EndY=8.28 EndZ=0
    g19: LineSegment StartX=24.5058 StartY=8.28 StartZ=0 EndX=25.5058 EndY=9.28 EndZ=0
    g20: LineSegment StartX=18.5058 StartY=8.28 StartZ=0 EndX=24.5058 EndY=8.28 EndZ=0
    g21: LineSegment [constr] StartX=21.5058 StartY=16.2884 StartZ=0 EndX=21.5058 EndY=2.78996 EndZ=0
  constraints (57):
    c: Coincident(g0,g1)
    c: Coincident(g2,g0)
    c: Horizontal(g0)
    c: Vertical(g1)
    c: Vertical(g2)
    c: Vertical(g3)
    c: Symmetric(g0,g0,g3)
    c: DistanceX(g0,g0) = 11.8
    c: Horizontal(g4)
    c: Horizontal(g5)
    c: Angle(g5,g6) = 2.44346
    c: Angle(g7,g5) = 2.44346
    c: Coincident(g2,g6)
    c: Coincident(g6,g5)
    c: DistanceY(g5,g2) = 1.2
    c: Coincident(g7,g5)
    c: DistanceY(g5,g7) = 1.2
    c: Coincident(g1,g7)
    c: DistanceY(g4,g5) = 1
    c: Coincident(g8,g9)
    c: Coincident(g10,g8)
    c: Horizontal(g8)
    c: Vertical(g9)
    c: Vertical(g10)
    c: DistanceX(g8,g8) = 8
    c: Vertical(g11)
    c: DistanceX(g3,g11) = 29.01
    c: Symmetric(g8,g8,g11)
    c: Horizontal(g14)
    c: DistanceY(g4,g14) = 0.78
    c: Angle(g13,g14) = 2.35619
    c: Angle(g14,g12) = 2.35619
    c: Coincident(g12,g14)
    c: Coincident(g12,g10)
    c: DistanceY(g12,g10) = 1
    c: Coincident(g14,g13)
    c: Coincident(g13,g9)
    c: DistanceY(g13,g9) = 1
    c: Coincident(g15,g16)
    c: Coincident(g17,g15)
    c: Horizontal(g15)
    c: Vertical(g16)
    c: Vertical(g17)
    c: Equal(g8,g15) = 7.8
    c: Horizontal(g20)
    c: Angle(g19,g20) = 2.35619
    c: Angle(g20,g18) = 2.35619
    c: Coincident(g18,g20)
    c: Coincident(g18,g17)
    c: DistanceY(g18,g17) = 1
    c: Coincident(g20,g19)
    c: Coincident(g19,g16)
    c: DistanceY(g19,g16) = 1
    c: DistanceY(g4,g18) = 0.78
    c: Vertical(g21)
    c: DistanceX(g11,g21) = 12.62
    c: Symmetric(g15,g15,g21)
FEATURE [PartDesign::Pocket] Pocket002
  BaseFeature = -> Pad002
  Length = 5
  Length2 = 100
  Profile = -> Sketch005
  Type = 2
FEATURE [Sketcher::SketchObject] Sketch006
  AttachmentOffset = pos=(0,-3.5,0) rot=(0,0,1;0rad)
  ExternalGeometry = -> [Pocket002]
  MapMode = 5
  Placement = pos=(-34.8,0,-3.5) rot=(0.57735,-0.57735,-0.57735;2.0944rad)
  Support = -> [Pocket002]
  sketch-geometry (12):
    g0: LineSegment [constr] StartX=-8.50001 StartY=7.5 StartZ=0 EndX=0.928937 EndY=7.5 EndZ=0
    g1: LineSegment [constr] StartX=-1.67421 StartY=13.4438 StartZ=0 EndX=-1.67421 EndY=3.80207 EndZ=0
    g2: LineSegment [constr] StartX=-11.4942 StartY=7.5 StartZ=0 EndX=-11.4942 EndY=14.033 EndZ=0
    g3: LineSegment StartX=4.62579 StartY=10.3 StartZ=0 EndX=4.62579 EndY=8.5 EndZ=0
    g4: LineSegment StartX=4.62579 StartY=8.5 StartZ=0 EndX=-7.97421 EndY=8.5 EndZ=0
    g5: LineSegment StartX=-7.97421 StartY=8.5 StartZ=0 EndX=-7.97421 EndY=10.3 EndZ=0
    g6: LineSegment [constr] StartX=4.62579 StartY=10.3 StartZ=0 EndX=-7.97421 EndY=10.3 EndZ=0
    g7: ArcOfEllipse CenterX=-1.67421 CenterY=10.3 CenterZ=0 NormalX=0 NormalY=0 NormalZ=1 MajorRadius=6.3 MinorRadius=1.00676 AngleXU=3.14159 StartAngle=3.14159 EndAngle=6.28319
    g8: LineSegment [constr] StartX=-7.97421 StartY=10.3 StartZ=0 EndX=4.62579 EndY=10.3 EndZ=0
    g9: LineSegment [constr] StartX=-1.67421 StartY=9.29324 StartZ=0 EndX=-1.67421 EndY=11.3068 EndZ=0
    g10: GeomPoint X=-7.89325 Y=10.3 Z=0
    g11: GeomPoint X=4.54482 Y=10.3 Z=0
FEATURE [PartDesign::Pocket] Pocket003
  BaseFeature = -> Pocket002
  Length = 5
  Length2 = 100
  Profile = -> Sketch006
  Type = 2
FEATURE [PartDesign::Chamfer] Chamfer
  Base = -> Pocket003 [Edge60,Edge62]
  BaseFeature = -> Pocket003
  Size = 0.6
FEATURE [Sketcher::SketchObject] Sketch007
  ExternalGeometry = -> [Chamfer]
  MapMode = 5
  Placement = pos=(0,0,10.5) rot=(0,0,1;0rad)
  Support = -> [Chamfer]
  sketch-geometry (4):
    g0: Circle CenterX=34.8 CenterY=17.3 CenterZ=0 NormalX=0 NormalY=0 NormalZ=1 AngleXU=0 Radius=2.43827
    g1: Circle CenterX=-34.8 CenterY=17.3 CenterZ=0 NormalX=0 NormalY=0 NormalZ=1 AngleXU=0 Radius=2.44385
    g2: Circle CenterX=-34.8 CenterY=-17.3 CenterZ=0 NormalX=0 NormalY=0 NormalZ=1 AngleXU=0 Radius=2.67402
    g3: Circle CenterX=34.8 CenterY=-17.3 CenterZ=0 NormalX=0 NormalY=0 NormalZ=1 AngleXU=0 Radius=2.67742
  constraints (4):
    c: Coincident(g0,g-3)
    c: Coincident(g1,g-4)
    c: Coincident(g2,g-6)
    c: Coincident(g3,g-5)
FEATURE [PartDesign::Hole] Hole
  BaseFeature = -> Chamfer
  Depth = 25
  DepthType = 1
  Diameter = 3.3
  DrillPoint = 1
  DrillPointAngle = 118
  HoleCutCountersinkAngle = 90
  HoleCutDepth = 0
  HoleCutDiameter = 3
  HoleCutType = 0
  ModelActualThread = false
  Profile = -> Sketch007
  Tapered = false
  TaperedAngle = 90
  ThreadAngle = 0
  ThreadClass = 0
  ThreadCutOffInner = 0
  ThreadCutOffOuter = 0
  ThreadDirection = 0
  ThreadFit = 0
  ThreadPitch = 0
  ThreadSize = 3
  ThreadType = 1
  Threaded = false
FEATURE [Sketcher::SketchObject] Sketch008
  ExternalGeometry = -> [Hole]
  MapMode = 5
  Placement = pos=(0,0,0) rot=(1,0,0;3.14159rad)
  Support = -> [Hole]
  sketch-geometry (32):
    g0: LineSegment [constr] StartX=-34.8 StartY=27.181 StartZ=0 EndX=-34.8 EndY=-26.8986 EndZ=0
    g1: LineSegment [constr] StartX=34.8 StartY=-24.6336 StartZ=0 EndX=34.8 EndY=23.8401 EndZ=0
    g2: LineSegment [constr] StartX=-45.3318 StartY=17.3 StartZ=0 EndX=42.1188 EndY=17.3 EndZ=0
    g3: LineSegment [constr] StartX=-44.7382 StartY=-17.3 StartZ=0 EndX=39.4916 EndY=-17.3 EndZ=0
    g4: LineSegment StartX=34.8 StartY=14.1708 StartZ=0 EndX=37.51 EndY=15.7354 EndZ=0
    g5: LineSegment StartX=37.51 StartY=15.7354 StartZ=0 EndX=37.51 EndY=18.8646 EndZ=0
    g6: LineSegment StartX=37.51 StartY=18.8646 StartZ=0 EndX=34.8 EndY=20.4292 EndZ=0
    g7: LineSegment StartX=34.8 StartY=20.4292 StartZ=0 EndX=32.09 EndY=18.8646 EndZ=0
    g8: LineSegment StartX=32.09 StartY=18.8646 StartZ=0 EndX=32.09 EndY=15.7354 EndZ=0
    g9: LineSegment StartX=32.09 StartY=15.7354 StartZ=0 EndX=34.8 EndY=14.1708 EndZ=0
    g10: Circle [constr] CenterX=34.8 CenterY=17.3 CenterZ=0 NormalX=0 NormalY=0 NormalZ=1 AngleXU=0 Radius=3.12924
    g11: LineSegment StartX=-34.8 StartY=14.1708 StartZ=0 EndX=-32.09 EndY=15.7354 EndZ=0
    g12: LineSegment StartX=-32.09 StartY=15.7354 StartZ=0 EndX=-32.09 EndY=18.8646 EndZ=0
    g13: LineSegment StartX=-32.09 StartY=18.8646 StartZ=0 EndX=-34.8 EndY=20.4292 EndZ=0
    g14: LineSegment StartX=-34.8 StartY=20.4292 StartZ=0 EndX=-37.51 EndY=18.8646 EndZ=0
    g15: LineSegment StartX=-37.51 StartY=18.8646 StartZ=0 EndX=-37.51 EndY=15.7354 EndZ=0
    g16: LineSegment StartX=-37.51 StartY=15.7354 StartZ=0 EndX=-34.8 EndY=14.1708 EndZ=0
    g17: Circle [constr] CenterX=-34.8 CenterY=17.3 CenterZ=0 NormalX=0 NormalY=0 NormalZ=1 AngleXU=0 Radius=3.12924
    g18: LineSegment StartX=34.8 StartY=-20.4292 StartZ=0 EndX=37.51 EndY=-18.8646 EndZ=0
    g19: LineSegment StartX=37.51 StartY=-18.8646 StartZ=0 EndX=37.51 EndY=-15.7354 EndZ=0
    g20: LineSegment StartX=37.51 StartY=-15.7354 StartZ=0 EndX=34.8 EndY=-14.1708 EndZ=0
    g21: LineSegment StartX=34.8 StartY=-14.1708 StartZ=0 EndX=32.09 EndY=-15.7354 EndZ=0
    g22: LineSegment StartX=32.09 StartY=-15.7354 StartZ=0 EndX=32.09 EndY=-18.8646 EndZ=0
    g23: LineSegment StartX=32.09 StartY=-18.8646 StartZ=0 EndX=34.8 EndY=-20.4292 EndZ=0
    g24: Circle [constr] CenterX=34.8 CenterY=-17.3 CenterZ=0 NormalX=0 NormalY=0 NormalZ=1 AngleXU=0 Radius=3.12924
    g25: LineSegment StartX=-34.8 StartY=-20.4292 StartZ=0 EndX=-32.09 EndY=-18.8646 EndZ=0
    g26: LineSegment StartX=-32.09 StartY=-18.8646 StartZ=0 EndX=-32.09 EndY=-15.7354 EndZ=0
    g27: LineSegment StartX=-32.09 StartY=-15.7354 StartZ=0 EndX=-34.8 EndY=-14.1708 EndZ=0
    g28: LineSegment StartX=-34.8 StartY=-14.1708 StartZ=0 EndX=-37.51 EndY=-15.7354 EndZ=0
    g29: LineSegment StartX=-37.51 StartY=-15.7354 StartZ=0 EndX=-37.51 EndY=-18.8646 EndZ=0
    g30: LineSegment StartX=-37.51 StartY=-18.8646 StartZ=0 EndX=-34.8 EndY=-20.4292 EndZ=0
    g31: Circle [constr] CenterX=-34.8 CenterY=-17.3 CenterZ=0 NormalX=0 NormalY=0 NormalZ=1 AngleXU=0 Radius=3.12924
  constraints (72):
    c: Vertical(g0)
    c: Vertical(g1)
    c: Horizontal(g2)
    c: Horizontal(g3)
    c: PointOnObject(g-6,g3)
    c: PointOnObject(g-6,g1)
    c: PointOnObject(g-5,g0)
    c: PointOnObject(g-4,g2)
    c: Coincident(g4,g5)
    c: Coincident(g5,g6)
    c: Coincident(g6,g7)
    c: Coincident(g7,g8)
    c: Coincident(g8,g9)
    c: Coincident(g9,g4)
    c: Equal(g4, g5-g9) x5
    c: PointOnObject(g4,g10)
    c: PointOnObject(g5,g10)
    c: PointOnObject(g6,g10)
    c: PointOnObject(g7,g10)
    c: PointOnObject(g8,g10)
    c: PointOnObject(g9,g10)
    c: Coincident(g10,g-3)
    c: PointOnObject(g9,g1)
    c: DistanceX(g7,g5) = 5.42
    c: Coincident(g11,g12)
    c: Coincident(g12,g13)
    c: Coincident(g13,g14)
    c: Coincident(g14,g15)
    c: Coincident(g15,g16)
    c: Coincident(g16,g11)
    c: Equal(g11, g12-g16) x5
    c: PointOnObject(g11,g17)
    c: PointOnObject(g12,g17)
    c: PointOnObject(g13,g17)
    c: PointOnObject(g14,g17)
    c: PointOnObject(g15,g17)
    c: PointOnObject(g16,g17)
    c: Coincident(g17,g-4)
    c: PointOnObject(g16,g0)
    c: DistanceX(g14,g12) = 5.42
    c: Coincident(g18,g19)
    c: Coincident(g19,g20)
    c: Coincident(g20,g21)
    c: Coincident(g21,g22)
    c: Coincident(g22,g23)
    c: Coincident(g23,g18)
    c: Equal(g18, g19-g23) x5
    c: PointOnObject(g18,g24)
    c: PointOnObject(g19,g24)
    c: PointOnObject(g20,g24)
    c: PointOnObject(g21,g24)
    c: PointOnObject(g22,g24)
    c: PointOnObject(g23,g24)
    c: Coincident(g24,g-6)
    c: PointOnObject(g23,g1)
    c: DistanceX(g21,g19) = 5.42
    c: Coincident(g25,g26)
    c: Coincident(g26,g27)
    c: Coincident(g27,g28)
    c: Coincident(g28,g29)
    c: Coincident(g29,g30)
    c: Coincident(g30,g25)
    c: Equal(g25, g26-g30) x5
    c: PointOnObject(g25,g31)
    c: PointOnObject(g26,g31)
    c: PointOnObject(g27,g31)
    c: PointOnObject(g28,g31)
    c: PointOnObject(g29,g31)
    c: PointOnObject(g30,g31)
    c: PointOnObject(g30,g0)
    c: DistanceX(g28,g26) = 5.42
    c: Coincident(g31,g-5)
FEATURE [PartDesign::Pocket] Pocket004
  BaseFeature = -> Hole
  Length = 5
  Length2 = 100
  Profile = -> Sketch008
  Type = 0
FEATURE [Sketcher::SketchObject] Sketch009
  MapMode = 5
  Placement = pos=(0,0,4) rot=(0,0,1;0rad)
  Support = -> [Pocket004]
  expr: Constraints[51] = Sketch.Constraints[51]
  expr: Constraints[49] = Sketch.Constraints[49]
  expr: Constraints[47] = Sketch.Constraints[47]
  expr: Constraints[40] = Sketch.Constraints[40]
  expr: Constraints[31] = Sketch.Constraints[31]
  expr: Constraints[30] = Sketch.Constraints[30]
  expr: Constraints[29] = Sketch.Constraints[29]
  expr: Constraints[28] = Sketch.Constraints[28]
  expr: Constraints[21] = Sketch.Constraints[21]
  expr: Constraints[20] = Sketch.Constraints[20]
  expr: Constraints[45] = Sketch.Constraints[45]
  expr: Constraints[43] = Sketch.Constraints[43]
  expr: Constraints[42] = Sketch.Constraints[42]
  expr: Constraints[41] = Sketch.Constraints[41]
  expr: Constraints[9] = Sketch.Constraints[9]
  expr: Constraints[8] = Sketch.Constraints[8]
  sketch-geometry (28):
    g0: LineSegment [constr] StartX=-32.5 StartY=15 StartZ=0 EndX=32.5 EndY=15 EndZ=0
    g1: LineSegment [constr] StartX=32.5 StartY=15 StartZ=0 EndX=32.5 EndY=-15 EndZ=0
    g2: LineSegment [constr] StartX=32.5 StartY=-15 StartZ=0 EndX=-32.5 EndY=-15 EndZ=0
    g3: LineSegment [constr] StartX=-32.5 StartY=-15 StartZ=0 EndX=-32.5 EndY=15 EndZ=0
    g4: LineSegment [constr] StartX=-29 StartY=11.5 StartZ=0 EndX=29 EndY=11.5 EndZ=0
    g5: LineSegment [constr] StartX=29 StartY=11.5 StartZ=0 EndX=29 EndY=-11.5 EndZ=0
    g6: LineSegment [constr] StartX=29 StartY=-11.5 StartZ=0 EndX=-29 EndY=-11.5 EndZ=0
    g7: LineSegment [constr] StartX=-29 StartY=-11.5 StartZ=0 EndX=-29 EndY=11.5 EndZ=0
    g8: Circle [constr] CenterX=-29 CenterY=11.5 CenterZ=0 NormalX=0 NormalY=0 NormalZ=1 AngleXU=0 Radius=1.375
    g9: Circle [constr] CenterX=29 CenterY=11.5 CenterZ=0 NormalX=0 NormalY=0 NormalZ=1 AngleXU=0 Radius=1.375
    g10: Circle [constr] CenterX=29 CenterY=-11.5 CenterZ=0 NormalX=0 NormalY=0 NormalZ=1 AngleXU=0 Radius=1.375
    g11: Circle [constr] CenterX=-29 CenterY=-11.5 CenterZ=0 NormalX=0 NormalY=0 NormalZ=1 AngleXU=0 Radius=1.375
    g12: LineSegment [constr] StartX=-29.5 StartY=12 StartZ=0 EndX=29.5 EndY=12 EndZ=0
    g13: LineSegment [constr] StartX=29.5 StartY=12 StartZ=0 EndX=29.5 EndY=-12 EndZ=0
    g14: LineSegment [constr] StartX=29.5 StartY=-12 StartZ=0 EndX=-29.5 EndY=-12 EndZ=0
    g15: LineSegment [constr] StartX=-29.5 StartY=-12 StartZ=0 EndX=-29.5 EndY=12 EndZ=0
    g16: ArcOfCircle [constr] CenterX=-29.5 CenterY=12 CenterZ=0 NormalX=0 NormalY=0 NormalZ=1 AngleXU=0 Radius=3 StartAngle=1.5708 EndAngle=3.14159
    g17: ArcOfCircle [constr] CenterX=29.5 CenterY=12 CenterZ=0 NormalX=0 NormalY=0 NormalZ=1 AngleXU=0 Radius=3 StartAngle=3.7568e-08 EndAngle=1.5708
    g18: ArcOfCircle [constr] CenterX=29.5 CenterY=-12 CenterZ=0 NormalX=0 NormalY=0 NormalZ=1 AngleXU=0 Radius=3 StartAngle=4.71239 EndAngle=6.28319
    g19: ArcOfCircle [constr] CenterX=-29.5 CenterY=-12 CenterZ=0 NormalX=0 NormalY=0 NormalZ=1 AngleXU=0 Radius=3 StartAngle=3.14159 EndAngle=4.71239
    g20: LineSegment [constr] StartX=-29.5 StartY=15 StartZ=0 EndX=29.5 EndY=15 EndZ=0
    g21: LineSegment [constr] StartX=32.5 StartY=12 StartZ=0 EndX=32.5 EndY=-12 EndZ=0
    g22: LineSegment [constr] StartX=29.5 StartY=-15 StartZ=0 EndX=-29.5 EndY=-15 EndZ=0
    g23: LineSegment [constr] StartX=-32.5 StartY=-12 StartZ=0 EndX=-32.5 EndY=12 EndZ=0
    g24: Circle CenterX=-29 CenterY=-11.5 CenterZ=0 NormalX=0 NormalY=0 NormalZ=1 AngleXU=0 Radius=1.07106
    g25: Circle CenterX=29 CenterY=-11.5 CenterZ=0 NormalX=0 NormalY=0 NormalZ=1 AngleXU=0 Radius=1.09378
    g26: Circle CenterX=29 CenterY=11.5 CenterZ=0 NormalX=0 NormalY=0 NormalZ=1 AngleXU=0 Radius=1.14533
    g27: Circle CenterX=-29 CenterY=11.5 CenterZ=0 NormalX=0 NormalY=0 NormalZ=1 AngleXU=0 Radius=1.23522
  constraints (72):
    c: Coincident(g0,g1)
    c: Coincident(g1,g2)
    c: Coincident(g2,g3)
    c: Coincident(g3,g0)
    c: Horizontal(g0)
    c: Horizontal(g2)
    c: Vertical(g1)
    c: Vertical(g3)
    c: DistanceX(g0,g0) = 65
    c: DistanceY(g1,g1) = 30
    c: Symmetric(g0,g0,g-2)
    c: Symmetric(g0,g1,g-1)
    c: Coincident(g4,g5)
    c: Coincident(g5,g6)
    c: Coincident(g6,g7)
    c: Coincident(g7,g4)
    c: Horizontal(g4)
    c: Horizontal(g6)
    c: Vertical(g5)
    c: Vertical(g7)
    c: DistanceX(g4,g4) = 58
    c: DistanceY(g5,g5) = 23
    c: Symmetric(g4,g5,g-1)
    c: Symmetric(g4,g4,g-2)
    c: Coincident(g8,g4)
    c: Coincident(g9,g4)
    c: Coincident(g10,g5)
    c: Coincident(g11,g6)
    c: Radius(g11) = 1.375
    c: Radius(g8) = 1.375
    c: Radius(g9) = 1.375
    c: Radius(g10) = 1.375
    c: Coincident(g12,g13)
    c: Coincident(g13,g14)
    c: Coincident(g14,g15)
    c: Coincident(g15,g12)
    c: Horizontal(g12)
    c: Horizontal(g14)
    c: Vertical(g13)
    c: Vertical(g15)
    c: DistanceX(g4,g12) = 0.5
    c: DistanceY(g4,g12) = 0.5
    c: DistanceY(g13,g5) = 0.5
    c: DistanceX(g14,g6) = 0.5
    c: Coincident(g16,g12)
    c: Radius(g16) = 3
    c: Coincident(g17,g12)
    c: Radius(g17) = 3
    c: Coincident(g18,g13)
    c: Radius(g18) = 3
    c: Coincident(g19,g14)
    c: Radius(g19) = 3
    c: PointOnObject(g16,g0)
    c: PointOnObject(g17,g1)
    c: PointOnObject(g18,g2)
    c: PointOnObject(g19,g3)
    c: Coincident(g20,g16)
    c: Horizontal(g20)
    c: Coincident(g20,g17)
    c: Coincident(g21,g17)
    c: Vertical(g21)
    c: Coincident(g18,g21)
    c: Coincident(g22,g18)
    c: Horizontal(g22)
    c: Coincident(g19,g22)
    c: Coincident(g23,g19)
    c: Vertical(g23)
    c: Coincident(g23,g16)
    c: Coincident(g24,g6)
    c: Coincident(g25,g5)
    c: Coincident(g26,g4)
    c: Coincident(g27,g4)
FEATURE [PartDesign::Hole] Hole001
  BaseFeature = -> Pocket004
  Depth = 25
  DepthType = 1
  Diameter = 2.2
  DrillPoint = 1
  DrillPointAngle = 118
  HoleCutCountersinkAngle = 90
  HoleCutDepth = 0
  HoleCutDiameter = 2
  HoleCutType = 0
  ModelActualThread = false
  Profile = -> Sketch009
  Tapered = false
  TaperedAngle = 90
  ThreadAngle = 60
  ThreadClass = 0
  ThreadCutOffInner = 0.0433013
  ThreadCutOffOuter = 0.0866025
  ThreadDirection = 0
  ThreadFit = 0
  ThreadPitch = 0.4
  ThreadSize = 1
  ThreadType = 1
  Threaded = false
FEATURE [Sketcher::SketchObject] Sketch010
  ExternalGeometry = -> [Hole001]
  MapMode = 5
  Placement = pos=(0,0,0) rot=(1,0,0;3.14159rad)
  Support = -> [Hole001]
  sketch-geometry (32):
    g0: LineSegment [constr] StartX=-29 StartY=20.1024 StartZ=0 EndX=-29 EndY=-21.8008 EndZ=0
    g1: LineSegment [constr] StartX=29 StartY=21.2945 StartZ=0 EndX=29 EndY=-21.3239 EndZ=0
    g2: LineSegment [constr] StartX=-40.5495 StartY=-11.5 StartZ=0 EndX=38.5479 EndY=-11.5 EndZ=0
    g3: LineSegment [constr] StartX=-40.9667 StartY=11.5 StartZ=0 EndX=41.409 EndY=11.5 EndZ=0
    g4: LineSegment StartX=29 StartY=9.13286 StartZ=0 EndX=31.05 EndY=10.3164 EndZ=0
    g5: LineSegment StartX=31.05 StartY=10.3164 StartZ=0 EndX=31.05 EndY=12.6836 EndZ=0
    g6: LineSegment StartX=31.05 StartY=12.6836 StartZ=0 EndX=29 EndY=13.8671 EndZ=0
    g7: LineSegment StartX=29 StartY=13.8671 StartZ=0 EndX=26.95 EndY=12.6836 EndZ=0
    g8: LineSegment StartX=26.95 StartY=12.6836 StartZ=0 EndX=26.95 EndY=10.3164 EndZ=0
    g9: LineSegment StartX=26.95 StartY=10.3164 StartZ=0 EndX=29 EndY=9.13286 EndZ=0
    g10: Circle [constr] CenterX=29 CenterY=11.5 CenterZ=0 NormalX=0 NormalY=0 NormalZ=1 AngleXU=0 Radius=2.36714
    g11: LineSegment StartX=-29 StartY=9.13286 StartZ=0 EndX=-26.95 EndY=10.3164 EndZ=0
    g12: LineSegment StartX=-26.95 StartY=10.3164 StartZ=0 EndX=-26.95 EndY=12.6836 EndZ=0
    g13: LineSegment StartX=-26.95 StartY=12.6836 StartZ=0 EndX=-29 EndY=13.8671 EndZ=0
    g14: LineSegment StartX=-29 StartY=13.8671 StartZ=0 EndX=-31.05 EndY=12.6836 EndZ=0
    g15: LineSegment StartX=-31.05 StartY=12.6836 StartZ=0 EndX=-31.05 EndY=10.3164 EndZ=0
    g16: LineSegment StartX=-31.05 StartY=10.3164 StartZ=0 EndX=-29 EndY=9.13286 EndZ=0
    g17: Circle [constr] CenterX=-29 CenterY=11.5 CenterZ=0 NormalX=0 NormalY=0 NormalZ=1 AngleXU=0 Radius=2.36714
    g18: LineSegment StartX=-29 StartY=-13.8671 StartZ=0 EndX=-26.95 EndY=-12.6836 EndZ=0
    g19: LineSegment StartX=-26.95 StartY=-12.6836 StartZ=0 EndX=-26.95 EndY=-10.3164 EndZ=0
    g20: LineSegment StartX=-26.95 StartY=-10.3164 StartZ=0 EndX=-29 EndY=-9.13286 EndZ=0
    g21: LineSegment StartX=-29 StartY=-9.13286 StartZ=0 EndX=-31.05 EndY=-10.3164 EndZ=0
    g22: LineSegment StartX=-31.05 StartY=-10.3164 StartZ=0 EndX=-31.05 EndY=-12.6836 EndZ=0
    g23: LineSegment StartX=-31.05 StartY=-12.6836 StartZ=0 EndX=-29 EndY=-13.8671 EndZ=0
    g24: Circle [constr] CenterX=-29 CenterY=-11.5 CenterZ=0 NormalX=0 NormalY=0 NormalZ=1 AngleXU=0 Radius=2.36714
    g25: LineSegment StartX=29 StartY=-13.8671 StartZ=0 EndX=31.05 EndY=-12.6836 EndZ=0
    g26: LineSegment StartX=31.05 StartY=-12.6836 StartZ=0 EndX=31.05 EndY=-10.3164 EndZ=0
    g27: LineSegment StartX=31.05 StartY=-10.3164 StartZ=0 EndX=29 EndY=-9.13286 EndZ=0
    g28: LineSegment StartX=29 StartY=-9.13286 StartZ=0 EndX=26.95 EndY=-10.3164 EndZ=0
    g29: LineSegment StartX=26.95 StartY=-10.3164 StartZ=0 EndX=26.95 EndY=-12.6836 EndZ=0
    g30: LineSegment StartX=26.95 StartY=-12.6836 StartZ=0 EndX=29 EndY=-13.8671 EndZ=0
    g31: Circle [constr] CenterX=29 CenterY=-11.5 CenterZ=0 NormalX=0 NormalY=0 NormalZ=1 AngleXU=0 Radius=2.36714
  constraints (72):
    c: Vertical(g0)
    c: Vertical(g1)
    c: Horizontal(g2)
    c: Horizontal(g3)
    c: PointOnObject(g-3,g3)
    c: PointOnObject(g-6,g2)
    c: PointOnObject(g-6,g1)
    c: PointOnObject(g-5,g0)
    c: Coincident(g4,g5)
    c: Coincident(g5,g6)
    c: Coincident(g6,g7)
    c: Coincident(g7,g8)
    c: Coincident(g8,g9)
    c: Coincident(g9,g4)
    c: Equal(g4, g5-g9) x5
    c: PointOnObject(g4,g10)
    c: PointOnObject(g5,g10)
    c: PointOnObject(g6,g10)
    c: PointOnObject(g7,g10)
    c: PointOnObject(g8,g10)
    c: PointOnObject(g9,g10)
    c: Coincident(g10,g-3)
    c: PointOnObject(g9,g1)
    c: DistanceX(g7,g5) = 4.1
    c: Coincident(g11,g12)
    c: Coincident(g12,g13)
    c: Coincident(g13,g14)
    c: Coincident(g14,g15)
    c: Coincident(g15,g16)
    c: Coincident(g16,g11)
    c: Equal(g11, g12-g16) x5
    c: PointOnObject(g11,g17)
    c: PointOnObject(g12,g17)
    c: PointOnObject(g13,g17)
    c: PointOnObject(g14,g17)
    c: PointOnObject(g15,g17)
    c: PointOnObject(g16,g17)
    c: Coincident(g17,g-4)
    c: PointOnObject(g16,g0)
    c: DistanceX(g14,g12) = 4.1
    c: Coincident(g18,g19)
    c: Coincident(g19,g20)
    c: Coincident(g20,g21)
    c: Coincident(g21,g22)
    c: Coincident(g22,g23)
    c: Coincident(g23,g18)
    c: Equal(g18, g19-g23) x5
    c: PointOnObject(g18,g24)
    c: PointOnObject(g19,g24)
    c: PointOnObject(g20,g24)
    c: PointOnObject(g21,g24)
    c: PointOnObject(g22,g24)
    c: PointOnObject(g23,g24)
    c: Coincident(g24,g-5)
    c: PointOnObject(g23,g0)
    c: DistanceX(g21,g19) = 4.1
    c: Coincident(g25,g26)
    c: Coincident(g26,g27)
    c: Coincident(g27,g28)
    c: Coincident(g28,g29)
    c: Coincident(g29,g30)
    c: Coincident(g30,g25)
    c: Equal(g25, g26-g30) x5
    c: PointOnObject(g25,g31)
    c: PointOnObject(g26,g31)
    c: PointOnObject(g27,g31)
    c: PointOnObject(g28,g31)
    c: PointOnObject(g29,g31)
    c: PointOnObject(g30,g31)
    c: Coincident(g31,g-6)
    c: PointOnObject(g30,g1)
    c: DistanceX(g28,g26) = 4.1
FEATURE [PartDesign::Pocket] Pocket005
  BaseFeature = -> Hole001
  Length = 2.5
  Length2 = 100
  Profile = -> Sketch010
  Type = 0
FEATURE [PartDesign::Fillet] Fillet
  Base = -> Pocket005 [Edge312,Edge306,Edge310,Edge308]
  BaseFeature = -> Pocket005
  Radius = 0.6
FEATURE [Sketcher::SketchObject] Sketch011
  ExternalGeometry = -> [Fillet]
  MapMode = 5
  Placement = pos=(32.8,0,0) rot=(0.57735,-0.57735,-0.57735;2.0944rad)
  Support = -> [Fillet]
  sketch-geometry (6):
    g0: LineSegment [constr] StartX=8.50001 StartY=4 StartZ=0 EndX=-8.09097 EndY=4 EndZ=0
    g1: LineSegment StartX=-9.5 StartY=8.5 StartZ=0 EndX=9.5 EndY=8.5 EndZ=0
    g2: LineSegment StartX=9.5 StartY=8.5 StartZ=0 EndX=9.5 EndY=5 EndZ=0
    g3: LineSegment StartX=9.5 StartY=5 StartZ=0 EndX=-9.5 EndY=5 EndZ=0
    g4: LineSegment StartX=-9.5 StartY=5 StartZ=0 EndX=-9.5 EndY=8.5 EndZ=0
    g5: LineSegment [constr] StartX=0 StartY=15.3767 StartZ=0 EndX=0 EndY=2.68391 EndZ=0
  constraints (16):
    c: Coincident(g0,g-3)
    c: Horizontal(g0)
    c: Coincident(g1,g2)
    c: Coincident(g2,g3)
    c: Coincident(g3,g4)
    c: Coincident(g4,g1)
    c: Horizontal(g1)
    c: Horizontal(g3)
    c: Vertical(g2)
    c: Vertical(g4)
    c: DistanceX(g1,g1) = 19
    c: PointOnObject(g5,g-2)
    c: Vertical(g5)
    c: Symmetric(g1,g1,g5)
    c: PointOnObject(g1,g-4)
    c: DistanceY(g0,g2) = 1
FEATURE [PartDesign::Pocket] Pocket006
  BaseFeature = -> Fillet
  Length = 0.7
  Length2 = 100
  Profile = -> Sketch011
  Type = 0
FEATURE [Sketcher::SketchObject] Sketch012
  ExternalGeometry = -> [Pocket006]
  MapMode = 5
  Placement = pos=(-32.8,0,0) rot=(0.57735,0.57735,0.57735;2.0944rad)
  Support = -> [Pocket006]
  sketch-geometry (15):
    g0: LineSegment [constr] StartX=8.97421 StartY=8.5 StartZ=0 EndX=8.97421 EndY=4.11024 EndZ=0
    g1: LineSegment [constr] StartX=-5.62579 StartY=8.5 StartZ=0 EndX=-5.62579 EndY=3.6342 EndZ=0
    g2: LineSegment [constr] StartX=-5.62579 StartY=8.5 StartZ=0 EndX=8.97421 EndY=8.5 EndZ=0
    g3: LineSegment [constr] StartX=8.17421 StartY=9.09588 StartZ=0 EndX=8.17421 EndY=3.57816 EndZ=0
    g4: LineSegment [constr] StartX=-4.72579 StartY=9.58242 StartZ=0 EndX=-4.72579 EndY=4.4197 EndZ=0
    g5: LineSegment [constr] StartX=-8.15183 StartY=7.7 StartZ=0 EndX=11.8659 EndY=7.7 EndZ=0
    g6: LineSegment [constr] StartX=-6.90186 StartY=7.4 StartZ=0 EndX=10.8983 EndY=7.4 EndZ=0
    g7: LineSegment StartX=-5.62579 StartY=8.5 StartZ=0 EndX=-1.62579 EndY=8.5 EndZ=0
    g8: LineSegment StartX=-1.62579 StartY=8.5 StartZ=0 EndX=-1.62579 EndY=7.4 EndZ=0
    g9: LineSegment StartX=-1.62579 StartY=7.4 StartZ=0 EndX=-5.62579 EndY=7.4 EndZ=0
    g10: LineSegment StartX=-5.62579 StartY=7.4 StartZ=0 EndX=-5.62579 EndY=8.5 EndZ=0
    g11: LineSegment StartX=8.97421 StartY=8.5 StartZ=0 EndX=4.97421 EndY=8.5 EndZ=0
    g12: LineSegment StartX=4.97421 StartY=8.5 StartZ=0 EndX=4.97421 EndY=7.4 EndZ=0
    g13: LineSegment StartX=4.97421 StartY=7.4 StartZ=0 EndX=8.97421 EndY=7.4 EndZ=0
    g14: LineSegment StartX=8.97421 StartY=7.4 StartZ=0 EndX=8.97421 EndY=8.5 EndZ=0
  constraints (38):
    c: Vertical(g0)
    c: DistanceX(g-4,g0) = 1
    c: Vertical(g1)
    c: DistanceX(g1,g-5) = 1
    c: PointOnObject(g2,g-7)
    c: Horizontal(g2)
    c: Vertical(g3)
    c: DistanceX(g3,g0) = 0.8
    c: Vertical(g4)
    c: DistanceX(g1,g4) = 0.9
    c: Horizontal(g5)
    c: DistanceY(g5,g2) = 0.8
    c: Horizontal(g6)
    c: DistanceY(g6,g-7) = 1.1
    c: Coincident(g1,g2)
    c: Coincident(g2,g0)
    c: Coincident(g7,g8)
    c: Coincident(g8,g9)
    c: Coincident(g9,g10)
    c: Coincident(g10,g7)
    c: Horizontal(g7)
    c: Horizontal(g9)
    c: Vertical(g8)
    c: Vertical(g10)
    c: Coincident(g7,g1)
    c: PointOnObject(g8,g6)
    c: Coincident(g11,g12)
    c: Coincident(g12,g13)
    c: Coincident(g13,g14)
    c: Coincident(g14,g11)
    c: Horizontal(g11)
    c: Horizontal(g13)
    c: Vertical(g12)
    c: Vertical(g14)
    c: Coincident(g11,g0)
    c: PointOnObject(g12,g6)
    c: DistanceX(g7,g7) = 4
    c: DistanceX(g11,g11) = 4
FEATURE [PartDesign::Pad] Pad003
  BaseFeature = -> Pocket006
  Length = 4
  Length2 = 100
  Profile = -> Sketch012
  Type = 0
FEATURE [Sketcher::SketchObject] Sketch013
  AttachmentOffset = pos=(0,0,-1.5) rot=(0,0,1;0rad)
  ExternalGeometry = -> [Pad003]
  MapMode = 5
  Placement = pos=(-30.3,0,0) rot=(0.57735,0.57735,0.57735;2.0944rad)
  Support = -> [Pad003]
  sketch-geometry (21):
    g0: LineSegment StartX=8.97421 StartY=7.4 StartZ=0 EndX=4.97421 EndY=7.4 EndZ=0
    g1: LineSegment StartX=4.97421 StartY=7.4 StartZ=0 EndX=4.97421 EndY=7.4 EndZ=0
    g2-g7: Circle [constr] x6 (B-spline internal-alignment scaffolding for g8; pole/knot coordinates omitted)
    g8: BSplineCurve PolesCount=6 KnotsCount=4 Degree=3 IsPeriodic=0
    g9-g12: GeomPoint [constr] x4 (B-spline internal-alignment scaffolding for g8; pole/knot coordinates omitted)
    g13: LineSegment StartX=4.97421 StartY=7.65732 StartZ=0 EndX=4.97421 EndY=7.4 EndZ=0
    g14: LineSegment [constr] StartX=1.67421 StartY=9.90728 StartZ=0 EndX=1.67421 EndY=2.98327 EndZ=0
    g15: LineSegment [constr] StartX=7.97421 StartY=6.8 StartZ=0 EndX=7.97421 EndY=5 EndZ=0
    g16: LineSegment [constr] StartX=-4.62579 StartY=5 StartZ=0 EndX=7.97421 EndY=5 EndZ=0
    g17: LineSegment StartX=-4.62579 StartY=6.8 StartZ=0 EndX=-4.62579 EndY=6.7 EndZ=0
    g18: LineSegment StartX=-4.62579 StartY=6.7 StartZ=0 EndX=-1.62579 EndY=6.7 EndZ=0
    g19: BSplineCurve PolesCount=6 KnotsCount=4 Degree=3 IsPeriodic=0
    g20: LineSegment StartX=-1.62579 StartY=7.65732 StartZ=0 EndX=-1.62579 EndY=6.7 EndZ=0
  constraints (22):
    c: Coincident(g-4,g0)
    c: Coincident(g0,g-4)
    c: Coincident(g0,g1)
    c: Coincident(g1,g-5)
    c: Coincident(g8,g0)
    c: Radius(g2) = 0.02
    c: Equal(g2, g3-g7) x5
    c: PointOnObject(g8,g-5)
    c: InternalAlignment(g2-g7 -> g8) x6
    c: InternalAlignment(g9-g12 -> g8) x4
    c: Coincident(g13,g8)
    c: Coincident(g13,g1)
    c: Vertical(g14)
    c: Coincident(g15,g-6)
    c: PointOnObject(g15,g-6)
    c: PointOnObject(g16,g-7)
    c: Coincident(g16,g-7)
    c: Symmetric(g15,g16,g14)
    c: Coincident(g17,g18)
    c: Coincident(g19,g17)
    c: Coincident(g20,g19)
    c: Coincident(g20,g18)
FEATURE [PartDesign::Pocket] Pocket007
  BaseFeature = -> Pad003
  Length = 2.5
  Length2 = 100
  Profile = -> Sketch013
  Type = 0
FEATURE [PartDesign::Fillet] Fillet001
  Base = -> Pocket007 [Edge443,Edge447]
  BaseFeature = -> Pocket007
  Radius = 0.2
FEATURE [PartDesign::Fillet] Fillet002
  Base = -> Fillet001 [Edge42,Edge19,Edge147,Edge105]
  BaseFeature = -> Fillet001
  Radius = 1
FEATURE [PartDesign::Fillet] Fillet003
  Base = -> Fillet002 [Edge26,Edge52,Edge15,Edge41]
  BaseFeature = -> Fillet002
  Radius = 2
FEATURE [PartDesign::Fillet] Fillet004
  Base = -> Fillet003 [Edge41,Edge182,Edge176,Edge88]
  BaseFeature = -> Fillet003
  Radius = 0.1
FEATURE [Sketcher::SketchObject] Sketch014
  ExternalGeometry = -> [Fillet004]
  MapMode = 5
  Placement = pos=(0,-17.3,0) rot=(1,0,0;1.5708rad)
  Support = -> [Fillet004]
  sketch-geometry (6):
    g0: LineSegment StartX=-26.0242 StartY=8.5 StartZ=0 EndX=-14.2242 EndY=8.5 EndZ=0
    g1: LineSegment StartX=-14.2242 StartY=8.5 StartZ=0 EndX=-14.2242 EndY=6.2 EndZ=0
    g2: LineSegment StartX=-14.2242 StartY=6.2 StartZ=0 EndX=-15.6543 EndY=5 EndZ=0
    g3: LineSegment StartX=-15.6543 StartY=5 StartZ=0 EndX=-24.5941 EndY=5 EndZ=0
    g4: LineSegment StartX=-24.5941 StartY=5 StartZ=0 EndX=-26.0242 EndY=6.2 EndZ=0
    g5: LineSegment StartX=-26.0242 StartY=6.2 StartZ=0 EndX=-26.0242 EndY=8.5 EndZ=0
  constraints (12):
    c: Coincident(g0,g-8)
    c: Coincident(g0,g-3)
    c: Coincident(g1,g0)
    c: Coincident(g1,g-4)
    c: Coincident(g2,g1)
    c: Coincident(g2,g-5)
    c: Coincident(g3,g2)
    c: Coincident(g3,g-6)
    c: Coincident(g4,g3)
    c: Coincident(g4,g-7)
    c: Coincident(g5,g4)
    c: Coincident(g5,g0)
FEATURE [PartDesign::Pad] Pad004
  BaseFeature = -> Fillet004
  Length = 1.5
  Length2 = 100
  Profile = -> Sketch014
  Reversed = true
  Type = 0
FEATURE [Sketcher::SketchObject] Sketch015
  ExternalGeometry = -> [Pad004]
  MapMode = 5
  Placement = pos=(0,-17.3,0) rot=(1,0,0;1.5708rad)
  Support = -> [Pad004]
  sketch-geometry (6):
    g0: LineSegment StartX=4.8858 StartY=8.5 StartZ=0 EndX=12.8858 EndY=8.5 EndZ=0
    g1: LineSegment StartX=12.8858 StartY=8.5 StartZ=0 EndX=12.8858 EndY=5.78 EndZ=0
    g2: LineSegment StartX=12.8858 StartY=5.78 StartZ=0 EndX=11.8858 EndY=4.78 EndZ=0
    g3: LineSegment StartX=11.8858 StartY=4.78 StartZ=0 EndX=5.8858 EndY=4.78 EndZ=0
    g4: LineSegment StartX=5.8858 StartY=4.78 StartZ=0 EndX=4.8858 EndY=5.78 EndZ=0
    g5: LineSegment StartX=4.8858 StartY=5.78 StartZ=0 EndX=4.8858 EndY=8.5 EndZ=0
  constraints (12):
    c: Coincident(g0,g-8)
    c: Coincident(g0,g-4)
    c: Coincident(g1,g0)
    c: Coincident(g1,g-5)
    c: Coincident(g2,g1)
    c: Coincident(g2,g-6)
    c: Coincident(g3,g2)
    c: Coincident(g3,g-7)
    c: Coincident(g4,g3)
    c: Coincident(g4,g-8)
    c: Coincident(g5,g4)
    c: Coincident(g5,g0)
FEATURE [PartDesign::Pad] Pad005
  BaseFeature = -> Pad004
  Length = 1
  Length2 = 100
  Profile = -> Sketch015
  Reversed = true
  Type = 0
FEATURE [PartDesign::Body] Body
  Group = -> [Sketch,Sketch001,Pad,Sketch002,Pocket,Sketch003,Pad001,Sketch004,Pad002,Sketch005,Pocket002,Sketch006,Pocket003,Chamfer,Sketch007,Hole,Sketch008,Pocket004,Sketch009,Hole001,Sketch010,Pocket005,Fillet,Sketch011,Pocket006,Sketch012,Pad003,Sketch013,Pocket007,Fillet001,Fillet002,Fillet003,Fillet004,Sketch014,Pad004,Sketch015,Pad005]
  Origin = -> Origin
  Tip = -> Pad005
FEATURE [Mesh::Feature] Mesh  label="Pad005 (Meshed)"
